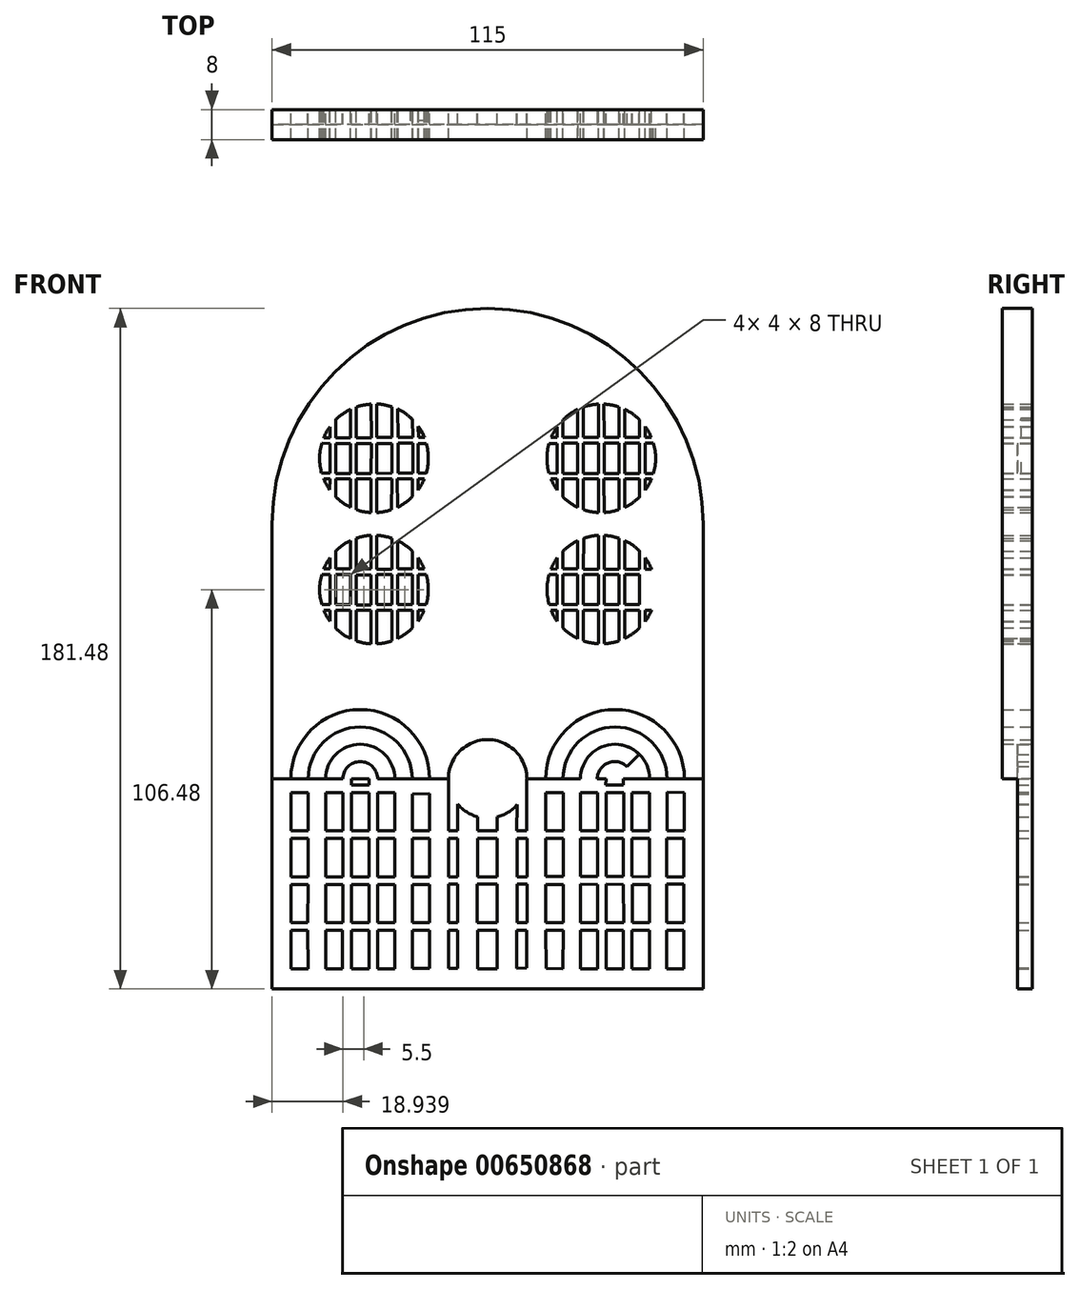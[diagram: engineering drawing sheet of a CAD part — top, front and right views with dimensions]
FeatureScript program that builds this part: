
annotation { "Feature Type Name" : "Feature", "Feature Type Description" : "" }
export const myFeature = defineFeature(function(context is Context, id is Id, definition is map)
    precondition{}
    {
        {
            var Q0;
            Q0=qCreatedBy(makeId("Front.planeOp"),FACE);
            var sketch = newSketch(context, id + "F0", { "sketchPlane" : qUnion([Q0])});
            skCircle(sketch, "E0", {"center": v(0, 0) * mm, "radius": 17.5 * mm});
            skPoint(sketch, "E1", {"position": v(0, 35) * mm});
            skPoint(sketch, "E2", {"position": v(-35, 0) * mm});
            skPoint(sketch, "E3", {"position": v(35, 0) * mm});
            skPoint(sketch, "E4", {"position": v(0, -35) * mm});
            skCircle(sketch, "E5", {"center": v(0, 0) * mm, "radius": 35 * mm});
            skPoint(sketch, "E6", {"position": v(-30.31, 17.5) * mm});
            skPoint(sketch, "E7", {"position": v(30.31, 17.5) * mm});
            skPoint(sketch, "E8", {"position": v(30.31, -17.5) * mm});
            skPoint(sketch, "E9", {"position": v(-30.31, -17.5) * mm});
            skCircle(sketch, "E10", {"center": v(-30.31, 17.5) * mm, "radius": 17.5 * mm});
            skCircle(sketch, "E11", {"center": v(30.31, 17.5) * mm, "radius": 17.5 * mm});
            skPoint(sketch, "E12", {"position": v(15.16, 8.75) * mm});
            skPoint(sketch, "E13", {"position": v(-15.16, -8.75) * mm});
            skCircle(sketch, "E14", {"center": v(-30.31, -17.5) * mm, "radius": 17.5 * mm});
            skCircle(sketch, "E15", {"center": v(0, -35) * mm, "radius": 17.5 * mm});
            skCircle(sketch, "E16", {"center": v(30.31, -17.5) * mm, "radius": 17.5 * mm});
            skCircle(sketch, "E17", {"center": v(0, 35) * mm, "radius": 17.5 * mm});
            skPoint(sketch, "E18", {"position": v(0, -52.5) * mm});
            skCircle(sketch, "E19", {"center": v(0, 0) * mm, "radius": 14.5 * mm});
            skCircle(sketch, "E20", {"center": v(-30.31, 17.5) * mm, "radius": 14.5 * mm});
            skCircle(sketch, "E21", {"center": v(0, 35) * mm, "radius": 14.5 * mm});
            skCircle(sketch, "E22", {"center": v(30.31, 17.5) * mm, "radius": 14.5 * mm});
            skCircle(sketch, "E23", {"center": v(30.31, -17.5) * mm, "radius": 14.5 * mm});
            skCircle(sketch, "E24", {"center": v(0, -35) * mm, "radius": 14.5 * mm});
            skCircle(sketch, "E25", {"center": v(-30.31, -17.5) * mm, "radius": 14.5 * mm});
            skArc(sketch, "E26", {"start": v(57.5, 0) * mm, "mid": v(0, 57.5) * mm, "end": v(-57.5, 0) * mm});
            skPoint(sketch, "E27", {"position": v(-20.96, 36.3) * mm});
            skArc(sketch, "E28", {"start": v(-20.96, 36.3) * mm, "mid": v(-28.74, 38.44) * mm, "end": v(-36.76, 37.49) * mm});
            skArc(sketch, "E29", {"start": v(-20.96, 36.3) * mm, "mid": v(-18.92, 44.11) * mm, "end": v(-14.09, 50.57) * mm});
            skPoint(sketch, "E30", {"position": v(14.09, 50.58) * mm});
            skPoint(sketch, "E31", {"position": v(41.92, 0) * mm});
            skArc(sketch, "E32", {"start": v(50.84, 13.09) * mm, "mid": v(47.66, 5.67) * mm, "end": v(41.92, 0) * mm});
            skArc(sketch, "E33", {"start": v(41.92, 0) * mm, "mid": v(47.66, -5.67) * mm, "end": v(50.84, -13.09) * mm});
            skPoint(sketch, "E34", {"position": v(20.96, 36.3) * mm});
            skArc(sketch, "E35", {"start": v(20.96, 36.3) * mm, "mid": v(28.74, 38.44) * mm, "end": v(36.76, 37.49) * mm});
            skArc(sketch, "E36", {"start": v(14.09, 50.58) * mm, "mid": v(18.92, 44.11) * mm, "end": v(20.96, 36.3) * mm});
            skArc(sketch, "E37", {"start": v(-50.84, -13.09) * mm, "mid": v(-47.66, -5.67) * mm, "end": v(-41.92, 0) * mm});
            skArc(sketch, "E38", {"start": v(-50.84, 13.09) * mm, "mid": v(-47.66, 5.67) * mm, "end": v(-41.92, 0) * mm});
            skArc(sketch, "E39", {"start": v(-50.84, -13.09) * mm, "mid": v(-52.5, 0) * mm, "end": v(-50.84, 13.09) * mm});
            skArc(sketch, "E40", {"start": v(-36.76, -37.49) * mm, "mid": v(-28.74, -38.44) * mm, "end": v(-20.96, -36.3) * mm});
            skArc(sketch, "E41", {"start": v(-20.96, -36.3) * mm, "mid": v(-18.92, -44.11) * mm, "end": v(-14.09, -50.58) * mm});
            skArc(sketch, "E42", {"start": v(-36.76, -37.49) * mm, "mid": v(-26.25, -45.47) * mm, "end": v(-14.09, -50.58) * mm});
            skArc(sketch, "E43", {"start": v(14.09, -50.58) * mm, "mid": v(18.92, -44.11) * mm, "end": v(20.96, -36.3) * mm});
            skArc(sketch, "E44", {"start": v(20.96, -36.3) * mm, "mid": v(28.74, -38.44) * mm, "end": v(36.76, -37.49) * mm});
            skArc(sketch, "E45", {"start": v(14.09, -50.58) * mm, "mid": v(26.25, -45.47) * mm, "end": v(36.76, -37.49) * mm});
            skArc(sketch, "E46", {"start": v(50.84, -13.09) * mm, "mid": v(52.5, 0) * mm, "end": v(50.84, 13.09) * mm, "construction": true});
            skArc(sketch, "E47", {"start": v(14.09, 50.58) * mm, "mid": v(26.25, 45.47) * mm, "end": v(36.76, 37.49) * mm});
            skArc(sketch, "E48", {"start": v(-36.76, 37.49) * mm, "mid": v(-26.25, 45.47) * mm, "end": v(-14.09, 50.58) * mm});
            skLineSegment(sketch, "E49", {"start": v(0, 0) * mm, "end": v(47.13, 81.64) * mm, "construction": true});
            skArc(sketch, "E50", {"start": v(50.84, 13.09) * mm, "mid": v(52.5, 0) * mm, "end": v(50.84, -13.09) * mm});
            skSolve(sketch);
        }
        {
            var Q0;
            Q0=qCreatedBy(makeId("Front.planeOp"),FACE);
            var sketch = newSketch(context, id + "F1", { "sketchPlane" : qUnion([Q0])});
            skArc(sketch, "E51", {"start": v(57.5, 0) * mm, "mid": v(0, 57.5) * mm, "end": v(-57.5, 0) * mm});
            skLineSegment(sketch, "E52", {"start": v(57.5, -67.99) * mm, "end": v(57.5, 0) * mm});
            skLineSegment(sketch, "E53", {"start": v(-57.5, 0) * mm, "end": v(-57.5, -67.99) * mm});
            skPoint(sketch, "E54", {"position": v(-52.5, -67.99) * mm});
            skLineSegment(sketch, "E55", {"start": v(-52.5, -67.99) * mm, "end": v(52.5, -67.99) * mm});
            skPoint(sketch, "E56", {"position": v(-52.5, -23.45) * mm});
            skLineSegment(sketch, "E57", {"start": v(-52.5, -23.45) * mm, "end": v(-52.5, -67.99) * mm});
            skLineSegment(sketch, "E58", {"start": v(52.5, -23.45) * mm, "end": v(52.5, -67.99) * mm});
            skArc(sketch, "E59", {"start": v(-52.5, -23.45) * mm, "mid": v(-31.29, -48.24) * mm, "end": v(0, -57.5) * mm});
            skArc(sketch, "E60", {"start": v(0, -57.5) * mm, "mid": v(31.29, -48.24) * mm, "end": v(52.5, -23.45) * mm});
            skArc(sketch, "E61", {"start": v(-15.48, -67.99) * mm, "mid": v(-33.99, -49.48) * mm, "end": v(-52.5, -67.99) * mm});
            skArc(sketch, "E62", {"start": v(52.5, -67.99) * mm, "mid": v(33.99, -49.48) * mm, "end": v(15.48, -67.99) * mm});
            skArc(sketch, "E63", {"start": v(-10.48, -67.99) * mm, "mid": v(0, -57.5) * mm, "end": v(10.48, -67.99) * mm});
            skLineSegment(sketch, "E64", {"start": v(-10.48, -67.99) * mm, "end": v(-10.48, -73.7) * mm, "construction": true});
            skLineSegment(sketch, "E65", {"start": v(10.48, -67.99) * mm, "end": v(10.48, -74.15) * mm, "construction": true});
            skLineSegment(sketch, "E66", {"start": v(15.48, -67.99) * mm, "end": v(15.48, -73.84) * mm, "construction": true});
            skLineSegment(sketch, "E67", {"start": v(52.5, -67.99) * mm, "end": v(52.5, -74.35) * mm, "construction": true});
            skLineSegment(sketch, "E68", {"start": v(-15.48, -67.99) * mm, "end": v(-15.48, -74.15) * mm, "construction": true});
            skLineSegment(sketch, "E69", {"start": v(-52.5, -67.99) * mm, "end": v(-52.5, -75.2) * mm, "construction": true});
            skLineSegment(sketch, "E70", {"start": v(-15.48, -72) * mm, "end": v(-10.48, -72) * mm, "construction": true});
            skLineSegment(sketch, "E71", {"start": v(10.48, -71.6) * mm, "end": v(15.49, -71.6) * mm, "construction": true});
            skLineSegment(sketch, "E72", {"start": v(52.5, -67.99) * mm, "end": v(57.5, -67.99) * mm, "construction": true});
            skLineSegment(sketch, "E73", {"start": v(-52.5, -67.99) * mm, "end": v(-57.5, -67.99) * mm, "construction": true});
            skCircle(sketch, "E74", {"center": v(0, 0) * mm, "radius": 57.5 * mm});
            skLineSegment(sketch, "E75", {"start": v(15.49, -71.6) * mm, "end": v(20.11, -71.6) * mm, "construction": true});
            skLineSegment(sketch, "E76", {"start": v(20.11, -71.6) * mm, "end": v(24.74, -71.6) * mm, "construction": true});
            skLineSegment(sketch, "E77", {"start": v(24.74, -71.6) * mm, "end": v(29.36, -71.6) * mm, "construction": true});
            skLineSegment(sketch, "E78", {"start": v(29.36, -71.6) * mm, "end": v(33.99, -71.6) * mm, "construction": true});
            skLineSegment(sketch, "E79", {"start": v(33.99, -71.6) * mm, "end": v(38.62, -71.6) * mm, "construction": true});
            skLineSegment(sketch, "E80", {"start": v(38.62, -71.6) * mm, "end": v(43.24, -71.6) * mm, "construction": true});
            skLineSegment(sketch, "E81", {"start": v(43.24, -71.6) * mm, "end": v(47.87, -71.6) * mm, "construction": true});
            skLineSegment(sketch, "E82", {"start": v(47.87, -71.6) * mm, "end": v(52.5, -71.6) * mm, "construction": true});
            skLineSegment(sketch, "E83", {"start": v(20.11, -71.6) * mm, "end": v(20.11, -67.99) * mm, "construction": true});
            skLineSegment(sketch, "E84", {"start": v(24.74, -71.6) * mm, "end": v(24.74, -67.99) * mm, "construction": true});
            skLineSegment(sketch, "E85", {"start": v(29.36, -71.6) * mm, "end": v(29.36, -67.99) * mm, "construction": true});
            skLineSegment(sketch, "E86", {"start": v(33.99, -71.6) * mm, "end": v(33.99, -67.99) * mm, "construction": true});
            skLineSegment(sketch, "E87", {"start": v(38.62, -71.6) * mm, "end": v(38.62, -67.99) * mm, "construction": true});
            skLineSegment(sketch, "E88", {"start": v(43.24, -71.6) * mm, "end": v(43.24, -67.99) * mm, "construction": true});
            skLineSegment(sketch, "E89", {"start": v(47.87, -71.6) * mm, "end": v(47.87, -67.99) * mm, "construction": true});
            skArc(sketch, "E90", {"start": v(47.87, -67.99) * mm, "mid": v(33.99, -54.1) * mm, "end": v(20.11, -67.99) * mm});
            skArc(sketch, "E91", {"start": v(43.24, -67.99) * mm, "mid": v(33.99, -58.74) * mm, "end": v(24.74, -67.99) * mm});
            skArc(sketch, "E92", {"start": v(38.62, -67.99) * mm, "mid": v(33.99, -63.36) * mm, "end": v(29.36, -67.99) * mm});
            skLineSegment(sketch, "E93", {"start": v(-15.48, -72) * mm, "end": v(-20.11, -72) * mm, "construction": true});
            skLineSegment(sketch, "E94", {"start": v(-20.11, -72) * mm, "end": v(-24.74, -72) * mm, "construction": true});
            skLineSegment(sketch, "E95", {"start": v(-24.74, -72) * mm, "end": v(-29.36, -72) * mm, "construction": true});
            skLineSegment(sketch, "E96", {"start": v(-29.36, -72) * mm, "end": v(-33.99, -72) * mm, "construction": true});
            skLineSegment(sketch, "E97", {"start": v(-33.99, -72) * mm, "end": v(-38.62, -72) * mm, "construction": true});
            skLineSegment(sketch, "E98", {"start": v(-38.62, -72) * mm, "end": v(-43.24, -72) * mm, "construction": true});
            skLineSegment(sketch, "E99", {"start": v(-43.24, -72) * mm, "end": v(-47.87, -72) * mm, "construction": true});
            skLineSegment(sketch, "E100", {"start": v(-47.87, -72) * mm, "end": v(-52.5, -72) * mm, "construction": true});
            skLineSegment(sketch, "E101", {"start": v(-47.87, -72) * mm, "end": v(-47.87, -67.99) * mm, "construction": true});
            skLineSegment(sketch, "E102", {"start": v(-43.24, -72) * mm, "end": v(-43.24, -67.99) * mm, "construction": true});
            skLineSegment(sketch, "E103", {"start": v(-38.62, -72) * mm, "end": v(-38.62, -67.99) * mm, "construction": true});
            skLineSegment(sketch, "E104", {"start": v(-29.36, -72) * mm, "end": v(-29.36, -67.99) * mm, "construction": true});
            skLineSegment(sketch, "E105", {"start": v(-24.74, -72) * mm, "end": v(-24.74, -67.99) * mm, "construction": true});
            skLineSegment(sketch, "E106", {"start": v(-20.11, -72) * mm, "end": v(-20.11, -67.99) * mm, "construction": true});
            skLineSegment(sketch, "E107", {"start": v(-33.99, -72) * mm, "end": v(-33.99, -67.99) * mm, "construction": true});
            skArc(sketch, "E108", {"start": v(-20.11, -67.99) * mm, "mid": v(-33.99, -54.1) * mm, "end": v(-47.87, -67.99) * mm});
            skArc(sketch, "E109", {"start": v(-24.74, -67.99) * mm, "mid": v(-33.99, -58.74) * mm, "end": v(-43.24, -67.99) * mm});
            skArc(sketch, "E110", {"start": v(-29.36, -67.99) * mm, "mid": v(-33.99, -63.36) * mm, "end": v(-38.62, -67.99) * mm});
            skLineSegment(sketch, "E111", {"start": v(-10.48, -72) * mm, "end": v(-7.86, -72) * mm, "construction": true});
            skLineSegment(sketch, "E112", {"start": v(-7.86, -72) * mm, "end": v(-5.24, -72) * mm, "construction": true});
            skLineSegment(sketch, "E113", {"start": v(-5.24, -72) * mm, "end": v(-2.62, -72) * mm, "construction": true});
            skLineSegment(sketch, "E114", {"start": v(-2.62, -72) * mm, "end": v(0, -72) * mm, "construction": true});
            skLineSegment(sketch, "E115", {"start": v(0, -72) * mm, "end": v(2.62, -72) * mm, "construction": true});
            skLineSegment(sketch, "E116", {"start": v(2.62, -72) * mm, "end": v(5.24, -72) * mm, "construction": true});
            skLineSegment(sketch, "E117", {"start": v(5.24, -72) * mm, "end": v(7.86, -72) * mm, "construction": true});
            skLineSegment(sketch, "E118", {"start": v(7.86, -72) * mm, "end": v(10.48, -72) * mm, "construction": true});
            skLineSegment(sketch, "E119", {"start": v(-7.86, -72) * mm, "end": v(-7.86, -67.99) * mm, "construction": true});
            skLineSegment(sketch, "E120", {"start": v(-5.24, -72) * mm, "end": v(-5.24, -67.99) * mm, "construction": true});
            skLineSegment(sketch, "E121", {"start": v(-2.62, -72) * mm, "end": v(-2.62, -67.99) * mm, "construction": true});
            skLineSegment(sketch, "E122", {"start": v(2.62, -72) * mm, "end": v(2.62, -67.99) * mm, "construction": true});
            skLineSegment(sketch, "E123", {"start": v(0, -72) * mm, "end": v(0, -67.98) * mm, "construction": true});
            skLineSegment(sketch, "E124", {"start": v(5.24, -72) * mm, "end": v(5.24, -67.99) * mm, "construction": true});
            skLineSegment(sketch, "E125", {"start": v(7.86, -72) * mm, "end": v(7.86, -67.99) * mm, "construction": true});
            skArc(sketch, "E126", {"start": v(7.86, -67.99) * mm, "mid": v(0, -60.13) * mm, "end": v(-7.86, -67.99) * mm});
            skArc(sketch, "E127", {"start": v(5.24, -67.99) * mm, "mid": v(0, -62.75) * mm, "end": v(-5.24, -67.99) * mm});
            skArc(sketch, "E128", {"start": v(2.62, -67.99) * mm, "mid": v(0, -65.37) * mm, "end": v(-2.62, -67.99) * mm});
            skLineSegment(sketch, "E129", {"start": v(-33.99, -67.99) * mm, "end": v(-33.99, -49.48) * mm, "construction": true});
            skLineSegment(sketch, "E130", {"start": v(33.99, -67.99) * mm, "end": v(33.99, -49.48) * mm, "construction": true});
            skLineSegment(sketch, "E131", {"start": v(0, -57.5) * mm, "end": v(0, -67.98) * mm, "construction": true});
            skLineSegment(sketch, "E132", {"start": v(-33.99, -67.99) * mm, "end": v(-47.08, -54.9) * mm, "construction": true});
            skLineSegment(sketch, "E133", {"start": v(-33.99, -67.99) * mm, "end": v(-20.9, -54.9) * mm, "construction": true});
            skLineSegment(sketch, "E134", {"start": v(33.99, -67.99) * mm, "end": v(20.9, -54.9) * mm, "construction": true});
            skLineSegment(sketch, "E135", {"start": v(33.99, -67.99) * mm, "end": v(47.08, -54.9) * mm, "construction": true});
            skLineSegment(sketch, "E136", {"start": v(0, -67.98) * mm, "end": v(7.41, -60.57) * mm, "construction": true});
            skLineSegment(sketch, "E137", {"start": v(0, -67.98) * mm, "end": v(-7.41, -60.57) * mm, "construction": true});
            skLineSegment(sketch, "E138", {"start": v(-57.5, -67.99) * mm, "end": v(-52.5, -67.99) * mm});
            skLineSegment(sketch, "E139", {"start": v(52.5, -67.99) * mm, "end": v(57.5, -67.99) * mm});
            skPoint(sketch, "E140", {"position": v(-29.56, -3.02) * mm});
            skPoint(sketch, "E141", {"position": v(-42.06, -21.5) * mm});
            skLineSegment(sketch, "E142.bottom", {"start": v(-40.56, -13.5) * mm, "end": v(-40.56, -13.5) * mm});
            skLineSegment(sketch, "E142.top", {"start": v(-40.56, -21.5) * mm, "end": v(-40.56, -21.5) * mm});
            skLineSegment(sketch, "E142.left", {"start": v(-40.56, -13.5) * mm, "end": v(-40.56, -21.5) * mm});
            skLineSegment(sketch, "E142.right", {"start": v(-40.56, -13.5) * mm, "end": v(-40.56, -21.5) * mm});
            skLineSegment(sketch, "E143.bottom", {"start": v(-36.56, -21.5) * mm, "end": v(-36.57, -21.5) * mm});
            skLineSegment(sketch, "E143.top", {"start": v(-36.56, -13.5) * mm, "end": v(-36.57, -13.5) * mm});
            skLineSegment(sketch, "E143.left", {"start": v(-36.57, -21.5) * mm, "end": v(-36.57, -13.5) * mm});
            skLineSegment(sketch, "E143.right", {"start": v(-36.56, -21.5) * mm, "end": v(-36.56, -13.5) * mm});
            skLineSegment(sketch, "E144.bottom", {"start": v(-35.06, -13.56) * mm, "end": v(-31.06, -13.56) * mm});
            skLineSegment(sketch, "E144.top", {"start": v(-35.06, -21.56) * mm, "end": v(-31.06, -21.56) * mm});
            skLineSegment(sketch, "E144.left", {"start": v(-35.06, -13.56) * mm, "end": v(-35.06, -21.56) * mm});
            skLineSegment(sketch, "E144.right", {"start": v(-31.06, -13.56) * mm, "end": v(-31.06, -21.56) * mm});
            skLineSegment(sketch, "E145.bottom", {"start": v(-29.56, -13.52) * mm, "end": v(-25.56, -13.52) * mm});
            skLineSegment(sketch, "E145.top", {"start": v(-29.56, -21.52) * mm, "end": v(-25.56, -21.52) * mm});
            skLineSegment(sketch, "E145.left", {"start": v(-29.56, -13.52) * mm, "end": v(-29.56, -21.52) * mm});
            skLineSegment(sketch, "E145.right", {"start": v(-25.56, -13.52) * mm, "end": v(-25.56, -21.52) * mm});
            skLineSegment(sketch, "E146.bottom", {"start": v(-24.06, -13.5) * mm, "end": v(-20.06, -13.5) * mm});
            skLineSegment(sketch, "E146.top", {"start": v(-24.06, -21.5) * mm, "end": v(-20.06, -21.5) * mm});
            skLineSegment(sketch, "E146.left", {"start": v(-24.06, -13.5) * mm, "end": v(-24.06, -21.5) * mm});
            skLineSegment(sketch, "E146.right", {"start": v(-20.06, -13.5) * mm, "end": v(-20.06, -21.5) * mm});
            skLineSegment(sketch, "E147.bottom", {"start": v(-40.56, -13.5) * mm, "end": v(-36.57, -13.5) * mm});
            skLineSegment(sketch, "E147.top", {"start": v(-40.56, -21.5) * mm, "end": v(-36.57, -21.5) * mm});
            skLineSegment(sketch, "E147.right", {"start": v(-36.57, -13.5) * mm, "end": v(-36.57, -21.5) * mm});
            skLineSegment(sketch, "E148.bottom", {"start": v(-35.06, -23) * mm, "end": v(-31.06, -23) * mm});
            skLineSegment(sketch, "E149.bottom", {"start": v(-29.56, -23) * mm, "end": v(-25.57, -23) * mm});
            skLineSegment(sketch, "E150", {"start": v(-40.56, -13.5) * mm, "end": v(-36.56, -13.5) * mm});
            skLineSegment(sketch, "E151", {"start": v(-40.56, -12) * mm, "end": v(-36.56, -12) * mm});
            skLineSegment(sketch, "E152", {"start": v(-29.56, -12.02) * mm, "end": v(-25.56, -12.02) * mm});
            skLineSegment(sketch, "E153", {"start": v(-24.06, -12) * mm, "end": v(-20.06, -12) * mm});
            skLineSegment(sketch, "E154", {"start": v(-35.3, -3.87) * mm, "end": v(-35.3, -3.86) * mm});
            skLineSegment(sketch, "E155", {"start": v(-40.56, -23) * mm, "end": v(-36.56, -23) * mm});
            skLineSegment(sketch, "E156", {"start": v(-44.24, -13.5) * mm, "end": v(-42.06, -13.5) * mm});
            skLineSegment(sketch, "E157", {"start": v(-42.06, -13.5) * mm, "end": v(-42.06, -21.5) * mm});
            skLineSegment(sketch, "E158", {"start": v(-18.56, -21.5) * mm, "end": v(-16.38, -21.5) * mm});
            skLineSegment(sketch, "E159", {"start": v(-18.56, -13.52) * mm, "end": v(-18.56, -21.5) * mm});
            skPoint(sketch, "E160", {"position": v(0, -124.5) * mm});
            skLineSegment(sketch, "E161", {"start": v(57.5, -124.17) * mm, "end": v(-57.5, -124.17) * mm});
            skArc(sketch, "E162", {"start": v(-44.24, -13.5) * mm, "mid": v(-44.8, -17.5) * mm, "end": v(-44.24, -21.51) * mm});
            skArc(sketch, "E163", {"start": v(-16.4, -13.5) * mm, "mid": v(-15.83, -17.5) * mm, "end": v(-16.39, -21.5) * mm});
            skPoint(sketch, "E164", {"position": v(-44.24, -21.5) * mm});
            skLineSegment(sketch, "E165", {"start": v(-44.24, -21.5) * mm, "end": v(-42.06, -21.5) * mm});
            skPoint(sketch, "E166", {"position": v(-36.56, -12) * mm});
            skLineSegment(sketch, "E167", {"start": v(-35.06, -12) * mm, "end": v(-31.06, -12) * mm});
            skPoint(sketch, "E168", {"position": v(-35.07, -3.8) * mm});
            skPoint(sketch, "E169", {"position": v(-31.07, -3.02) * mm});
            skArc(sketch, "E170", {"start": v(-35.07, -3.8) * mm, "mid": v(-33.1, -3.28) * mm, "end": v(-31.07, -3.03) * mm});
            skArc(sketch, "E171", {"start": v(-29.56, -3.02) * mm, "mid": v(-27.53, -3.27) * mm, "end": v(-25.56, -3.8) * mm});
            skPoint(sketch, "E172", {"position": v(-36.57, -4.42) * mm});
            skPoint(sketch, "E173", {"position": v(-24.06, -4.41) * mm});
            skLineSegment(sketch, "E174", {"start": v(-20.07, -7.24) * mm, "end": v(-20.06, -12) * mm});
            skPoint(sketch, "E175", {"position": v(-18.57, -12) * mm});
            skPoint(sketch, "E176", {"position": v(-18.56, -9.01) * mm});
            skPoint(sketch, "E177", {"position": v(-16.92, -12) * mm});
            skLineSegment(sketch, "E178", {"start": v(-18.56, -9.01) * mm, "end": v(-18.57, -12) * mm});
            skPoint(sketch, "E179", {"position": v(-42.06, -9) * mm});
            skPoint(sketch, "E180", {"position": v(-42.06, -12) * mm});
            skPoint(sketch, "E181", {"position": v(-43.72, -12) * mm});
            skLineSegment(sketch, "E182", {"start": v(-43.72, -12) * mm, "end": v(-42.06, -12) * mm});
            skLineSegment(sketch, "E183", {"start": v(-42.06, -12) * mm, "end": v(-42.06, -9) * mm});
            skArc(sketch, "E184", {"start": v(-43.72, -12) * mm, "mid": v(-42.98, -10.47) * mm, "end": v(-42.06, -9.03) * mm});
            skArc(sketch, "E185", {"start": v(-18.56, -9.01) * mm, "mid": v(-17.64, -10.46) * mm, "end": v(-16.9, -12) * mm});
            skPoint(sketch, "E186", {"position": v(-42.06, -25.98) * mm});
            skPoint(sketch, "E187", {"position": v(-42.09, -23) * mm});
            skPoint(sketch, "E188", {"position": v(-43.7, -23) * mm});
            skLineSegment(sketch, "E189", {"start": v(-43.7, -23) * mm, "end": v(-42.09, -23) * mm});
            skLineSegment(sketch, "E190", {"start": v(-42.09, -23) * mm, "end": v(-42.06, -25.98) * mm});
            skArc(sketch, "E191", {"start": v(-43.7, -23) * mm, "mid": v(-42.97, -24.52) * mm, "end": v(-42.06, -25.94) * mm});
            skPoint(sketch, "E192", {"position": v(-31.07, -31.97) * mm});
            skPoint(sketch, "E193", {"position": v(-25.56, -31.19) * mm});
            skPoint(sketch, "E194", {"position": v(-20.06, -27.74) * mm});
            skLineSegment(sketch, "E195", {"start": v(-24.06, -23) * mm, "end": v(-20.06, -23) * mm});
            skPoint(sketch, "E196", {"position": v(-18.56, -22.98) * mm});
            skPoint(sketch, "E197", {"position": v(-16.92, -22.98) * mm});
            skPoint(sketch, "E198", {"position": v(-18.56, -25.95) * mm});
            skLineSegment(sketch, "E199", {"start": v(-18.56, -25.95) * mm, "end": v(-18.56, -22.98) * mm});
            skArc(sketch, "E200", {"start": v(-16.92, -22.98) * mm, "mid": v(-17.65, -24.51) * mm, "end": v(-18.56, -25.95) * mm});
            skLineSegment(sketch, "E201", {"start": v(-18.56, -22.98) * mm, "end": v(-16.92, -22.98) * mm});
            skPoint(sketch, "E202", {"position": v(-35.06, -31.2) * mm});
            skLineSegment(sketch, "E203", {"start": v(-18.57, -12) * mm, "end": v(-16.9, -12) * mm});
            skPoint(sketch, "E204", {"position": v(-24.06, -30.58) * mm});
            skArc(sketch, "E205", {"start": v(-31.07, -31.97) * mm, "mid": v(-33.1, -31.72) * mm, "end": v(-35.06, -31.2) * mm});
            skPoint(sketch, "E206", {"position": v(-29.56, -31.97) * mm});
            skArc(sketch, "E207", {"start": v(-25.56, -31.19) * mm, "mid": v(-27.53, -31.72) * mm, "end": v(-29.56, -31.97) * mm});
            skLineSegment(sketch, "E208", {"start": v(-35.07, -3.8) * mm, "end": v(-35.06, -12) * mm});
            skLineSegment(sketch, "E209", {"start": v(-31.07, -3.02) * mm, "end": v(-31.06, -12) * mm});
            skLineSegment(sketch, "E210", {"start": v(-29.56, -3.02) * mm, "end": v(-29.56, -12.02) * mm});
            skPoint(sketch, "E211", {"position": v(-25.56, -3.8) * mm});
            skLineSegment(sketch, "E212", {"start": v(-25.56, -3.8) * mm, "end": v(-25.56, -12.02) * mm});
            skPoint(sketch, "E213", {"position": v(-40.56, -7.25) * mm});
            skLineSegment(sketch, "E214", {"start": v(-36.57, -4.42) * mm, "end": v(-36.56, -12) * mm});
            skLineSegment(sketch, "E215", {"start": v(-40.56, -7.25) * mm, "end": v(-40.56, -12) * mm});
            skArc(sketch, "E216", {"start": v(-40.56, -7.25) * mm, "mid": v(-38.69, -5.66) * mm, "end": v(-36.57, -4.42) * mm});
            skArc(sketch, "E217", {"start": v(-24.06, -4.41) * mm, "mid": v(-21.94, -5.66) * mm, "end": v(-20.07, -7.25) * mm});
            skLineSegment(sketch, "E218", {"start": v(-24.06, -4.41) * mm, "end": v(-24.06, -12) * mm});
            skLineSegment(sketch, "E219", {"start": v(-20.07, -7.25) * mm, "end": v(-20.06, -12) * mm});
            skPoint(sketch, "E220", {"position": v(-40.56, -27.75) * mm});
            skPoint(sketch, "E221", {"position": v(-36.57, -30.57) * mm});
            skLineSegment(sketch, "E222", {"start": v(-40.56, -23) * mm, "end": v(-40.56, -27.75) * mm});
            skLineSegment(sketch, "E223", {"start": v(-36.56, -23) * mm, "end": v(-36.57, -30.57) * mm});
            skArc(sketch, "E224", {"start": v(-40.56, -27.75) * mm, "mid": v(-38.69, -29.33) * mm, "end": v(-36.57, -30.57) * mm});
            skLineSegment(sketch, "E225", {"start": v(-35.06, -23) * mm, "end": v(-35.06, -31.2) * mm});
            skLineSegment(sketch, "E226", {"start": v(-31.06, -23) * mm, "end": v(-31.07, -31.97) * mm});
            skLineSegment(sketch, "E227", {"start": v(-29.56, -23) * mm, "end": v(-29.56, -31.97) * mm});
            skLineSegment(sketch, "E228", {"start": v(-25.57, -23) * mm, "end": v(-25.56, -31.19) * mm});
            skLineSegment(sketch, "E229", {"start": v(-24.06, -23) * mm, "end": v(-24.06, -30.58) * mm});
            skLineSegment(sketch, "E230", {"start": v(-20.06, -23) * mm, "end": v(-20.06, -27.74) * mm});
            skArc(sketch, "E231", {"start": v(-20.06, -27.74) * mm, "mid": v(-21.94, -29.32) * mm, "end": v(-24.06, -30.57) * mm});
            skPoint(sketch, "E232", {"position": v(-42.1, 21.5) * mm});
            skPoint(sketch, "E233", {"position": v(-44.82, 17.5) * mm});
            skPoint(sketch, "E234", {"position": v(-42.08, 17.5) * mm});
            skPoint(sketch, "E235", {"position": v(-40.57, 17.5) * mm});
            skPoint(sketch, "E236", {"position": v(-42.07, 23) * mm});
            skPoint(sketch, "E237", {"position": v(-44.24, 21.53) * mm});
            skPoint(sketch, "E238", {"position": v(-43.74, 23) * mm});
            skLineSegment(sketch, "E239", {"start": v(-43.74, 23) * mm, "end": v(-42.07, 23) * mm});
            skLineSegment(sketch, "E240", {"start": v(-44.24, 21.53) * mm, "end": v(-42.1, 21.5) * mm});
            skLineSegment(sketch, "E241", {"start": v(-40.57, 23) * mm, "end": v(-36.56, 23) * mm});
            skLineSegment(sketch, "E242", {"start": v(-40.57, 21.5) * mm, "end": v(-36.56, 21.5) * mm});
            skLineSegment(sketch, "E243", {"start": v(-35.07, 23.04) * mm, "end": v(-31.04, 23.04) * mm});
            skLineSegment(sketch, "E244", {"start": v(-35.07, 21.5) * mm, "end": v(-31.04, 21.5) * mm});
            skLineSegment(sketch, "E245", {"start": v(-35.07, 31.2) * mm, "end": v(-35.07, 23.04) * mm});
            skLineSegment(sketch, "E246", {"start": v(-36.54, 30.6) * mm, "end": v(-36.56, 23) * mm});
            skPoint(sketch, "E247", {"position": v(-40.56, 27.8) * mm});
            skPoint(sketch, "E248", {"position": v(-42.08, 25.99) * mm});
            skLineSegment(sketch, "E249", {"start": v(-40.56, 27.8) * mm, "end": v(-40.57, 23) * mm});
            skLineSegment(sketch, "E250", {"start": v(-42.08, 25.99) * mm, "end": v(-42.07, 23) * mm});
            skPoint(sketch, "E251", {"position": v(-40.57, 13.5) * mm});
            skPoint(sketch, "E252", {"position": v(-36.58, 13.5) * mm});
            skPoint(sketch, "E253", {"position": v(-35.07, 13.5) * mm});
            skPoint(sketch, "E254", {"position": v(-31.08, 13.5) * mm});
            skPoint(sketch, "E255", {"position": v(-29.54, 13.5) * mm});
            skLineSegment(sketch, "E256", {"start": v(-40.57, 21.5) * mm, "end": v(-40.57, 13.5) * mm});
            skLineSegment(sketch, "E257", {"start": v(-36.56, 21.5) * mm, "end": v(-36.58, 13.5) * mm});
            skLineSegment(sketch, "E258", {"start": v(-35.07, 21.5) * mm, "end": v(-35.07, 13.5) * mm});
            skLineSegment(sketch, "E259", {"start": v(-31.04, 21.5) * mm, "end": v(-31.08, 13.5) * mm});
            skLineSegment(sketch, "E260", {"start": v(-40.57, 13.5) * mm, "end": v(-36.58, 13.5) * mm});
            skLineSegment(sketch, "E261", {"start": v(-35.07, 13.5) * mm, "end": v(-31.08, 13.5) * mm});
            skPoint(sketch, "E262", {"position": v(-44.27, 13.52) * mm});
            skPoint(sketch, "E263", {"position": v(-42.07, 13.52) * mm});
            skLineSegment(sketch, "E264", {"start": v(-44.27, 13.52) * mm, "end": v(-42.07, 13.52) * mm});
            skPoint(sketch, "E265", {"position": v(-29.6, 23.04) * mm});
            skPoint(sketch, "E266", {"position": v(-29.6, 21.5) * mm});
            skPoint(sketch, "E267", {"position": v(-25.47, 23.1) * mm});
            skPoint(sketch, "E268", {"position": v(-23.93, 23.1) * mm});
            skPoint(sketch, "E269", {"position": v(-19.94, 23.1) * mm});
            skPoint(sketch, "E270", {"position": v(-16.82, 23.1) * mm});
            skPoint(sketch, "E271", {"position": v(-18.46, 23.1) * mm});
            skPoint(sketch, "E272", {"position": v(-25.47, 21.5) * mm});
            skPoint(sketch, "E273", {"position": v(-23.93, 21.55) * mm});
            skPoint(sketch, "E274", {"position": v(-19.94, 21.55) * mm});
            skPoint(sketch, "E275", {"position": v(-18.57, 21.5) * mm});
            skPoint(sketch, "E276", {"position": v(-16.39, 21.5) * mm});
            skPoint(sketch, "E277", {"position": v(-25.47, 13.58) * mm});
            skPoint(sketch, "E278", {"position": v(-23.93, 13.58) * mm});
            skPoint(sketch, "E279", {"position": v(-19.94, 13.58) * mm});
            skPoint(sketch, "E280", {"position": v(-18.57, 13.52) * mm});
            skPoint(sketch, "E281", {"position": v(-16.35, 13.53) * mm});
            skLineSegment(sketch, "E282", {"start": v(-29.6, 23.04) * mm, "end": v(-25.47, 23.1) * mm});
            skLineSegment(sketch, "E283", {"start": v(-23.93, 23.1) * mm, "end": v(-19.94, 23.1) * mm});
            skLineSegment(sketch, "E284", {"start": v(-18.46, 23.1) * mm, "end": v(-16.82, 23.1) * mm});
            skLineSegment(sketch, "E285", {"start": v(-29.6, 21.5) * mm, "end": v(-25.47, 21.5) * mm});
            skLineSegment(sketch, "E286", {"start": v(-23.93, 21.55) * mm, "end": v(-19.94, 21.55) * mm});
            skLineSegment(sketch, "E287", {"start": v(-18.57, 21.5) * mm, "end": v(-16.39, 21.5) * mm});
            skLineSegment(sketch, "E288", {"start": v(-29.54, 13.5) * mm, "end": v(-25.47, 13.58) * mm});
            skLineSegment(sketch, "E289", {"start": v(-23.93, 13.58) * mm, "end": v(-19.94, 13.58) * mm});
            skLineSegment(sketch, "E290", {"start": v(-29.6, 21.5) * mm, "end": v(-29.54, 13.5) * mm});
            skLineSegment(sketch, "E291", {"start": v(-25.47, 21.5) * mm, "end": v(-25.47, 13.58) * mm});
            skLineSegment(sketch, "E292", {"start": v(-23.93, 21.55) * mm, "end": v(-23.93, 13.58) * mm});
            skLineSegment(sketch, "E293", {"start": v(-19.94, 21.55) * mm, "end": v(-19.94, 13.58) * mm});
            skLineSegment(sketch, "E294", {"start": v(-18.57, 21.5) * mm, "end": v(-18.57, 13.52) * mm});
            skPoint(sketch, "E295", {"position": v(-40.57, 12) * mm});
            skPoint(sketch, "E296", {"position": v(-36.59, 12.05) * mm});
            skPoint(sketch, "E297", {"position": v(-35.07, 12.05) * mm});
            skPoint(sketch, "E298", {"position": v(-31.08, 12.05) * mm});
            skPoint(sketch, "E299", {"position": v(-29.56, 12.05) * mm});
            skPoint(sketch, "E300", {"position": v(-25.55, 12.05) * mm});
            skPoint(sketch, "E301", {"position": v(-24.08, 12.05) * mm});
            skPoint(sketch, "E302", {"position": v(-20.06, 12.05) * mm});
            skPoint(sketch, "E303", {"position": v(-18.6, 12.05) * mm});
            skPoint(sketch, "E304", {"position": v(-16.9, 12.05) * mm});
            skPoint(sketch, "E305", {"position": v(-40.57, 7.3) * mm});
            skPoint(sketch, "E306", {"position": v(-36.6, 4.43) * mm});
            skPoint(sketch, "E307", {"position": v(-35.09, 3.8) * mm});
            skPoint(sketch, "E308", {"position": v(-31.1, 3.06) * mm});
            skPoint(sketch, "E309", {"position": v(-29.56, 3.05) * mm});
            skPoint(sketch, "E310", {"position": v(-25.6, 3.8) * mm});
            skPoint(sketch, "E311", {"position": v(-24.05, 4.43) * mm});
            skPoint(sketch, "E312", {"position": v(-20.07, 7.3) * mm});
            skPoint(sketch, "E313", {"position": v(-18.54, 9.06) * mm});
            skLineSegment(sketch, "E314", {"start": v(-40.57, 12) * mm, "end": v(-36.59, 12.05) * mm});
            skLineSegment(sketch, "E315", {"start": v(-35.07, 12.05) * mm, "end": v(-31.08, 12.05) * mm});
            skLineSegment(sketch, "E316", {"start": v(-29.56, 12.05) * mm, "end": v(-25.55, 12.05) * mm});
            skLineSegment(sketch, "E317", {"start": v(-24.08, 12.05) * mm, "end": v(-20.06, 12.05) * mm});
            skLineSegment(sketch, "E318", {"start": v(-18.6, 12.05) * mm, "end": v(-16.9, 12.05) * mm});
            skLineSegment(sketch, "E319", {"start": v(-40.57, 12) * mm, "end": v(-40.57, 7.3) * mm});
            skLineSegment(sketch, "E320", {"start": v(-36.59, 12.05) * mm, "end": v(-36.6, 4.43) * mm});
            skLineSegment(sketch, "E321", {"start": v(-35.07, 12.05) * mm, "end": v(-35.09, 3.8) * mm});
            skLineSegment(sketch, "E322", {"start": v(-31.08, 12.05) * mm, "end": v(-31.1, 3.06) * mm});
            skLineSegment(sketch, "E323", {"start": v(-29.56, 12.05) * mm, "end": v(-29.56, 3.05) * mm});
            skLineSegment(sketch, "E324", {"start": v(-25.55, 12.05) * mm, "end": v(-25.6, 3.8) * mm});
            skLineSegment(sketch, "E325", {"start": v(-24.08, 12.05) * mm, "end": v(-24.05, 4.43) * mm});
            skLineSegment(sketch, "E326", {"start": v(-20.06, 12.05) * mm, "end": v(-20.07, 7.3) * mm});
            skLineSegment(sketch, "E327", {"start": v(-18.6, 12.05) * mm, "end": v(-18.54, 9.06) * mm});
            skPoint(sketch, "E328", {"position": v(-29.58, 32.04) * mm});
            skPoint(sketch, "E329", {"position": v(-25.55, 31.25) * mm});
            skPoint(sketch, "E330", {"position": v(-23.98, 30.68) * mm});
            skPoint(sketch, "E331", {"position": v(-18.49, 26.07) * mm});
            skLineSegment(sketch, "E332", {"start": v(-29.58, 32.04) * mm, "end": v(-29.6, 23.04) * mm});
            skLineSegment(sketch, "E333", {"start": v(-23.98, 30.68) * mm, "end": v(-23.93, 23.1) * mm});
            skLineSegment(sketch, "E334", {"start": v(-18.49, 26.07) * mm, "end": v(-18.46, 23.1) * mm});
            skArc(sketch, "E335", {"start": v(-44.27, 13.52) * mm, "mid": v(-44.81, 17.53) * mm, "end": v(-44.22, 21.53) * mm});
            skArc(sketch, "E336", {"start": v(-43.74, 23) * mm, "mid": v(-43, 24.53) * mm, "end": v(-42.08, 25.96) * mm});
            skArc(sketch, "E337", {"start": v(-40.56, 27.8) * mm, "mid": v(-38.67, 29.37) * mm, "end": v(-36.54, 30.6) * mm});
            skArc(sketch, "E338", {"start": v(-35.07, 31.2) * mm, "mid": v(-33.1, 31.71) * mm, "end": v(-31.08, 31.95) * mm});
            skArc(sketch, "E339", {"start": v(-29.58, 32.04) * mm, "mid": v(-27.56, 31.79) * mm, "end": v(-25.6, 31.25) * mm});
            skArc(sketch, "E340", {"start": v(-23.98, 30.68) * mm, "mid": v(-21.88, 29.43) * mm, "end": v(-20.01, 27.86) * mm});
            skArc(sketch, "E341", {"start": v(-18.49, 26.07) * mm, "mid": v(-17.57, 24.63) * mm, "end": v(-16.82, 23.1) * mm});
            skArc(sketch, "E342", {"start": v(-16.39, 21.5) * mm, "mid": v(-15.81, 17.52) * mm, "end": v(-16.35, 13.53) * mm});
            skArc(sketch, "E343", {"start": v(-44.22, 21.53) * mm, "mid": v(-44.81, 17.53) * mm, "end": v(-44.27, 13.52) * mm});
            skArc(sketch, "E344", {"start": v(-40.57, 7.3) * mm, "mid": v(-38.7, 5.72) * mm, "end": v(-36.6, 4.48) * mm});
            skArc(sketch, "E345", {"start": v(-29.56, 3.05) * mm, "mid": v(-27.55, 3.3) * mm, "end": v(-25.6, 3.85) * mm});
            skArc(sketch, "E346", {"start": v(-24.05, 4.43) * mm, "mid": v(-21.94, 5.7) * mm, "end": v(-20.07, 7.3) * mm});
            skArc(sketch, "E347", {"start": v(-18.54, 9.06) * mm, "mid": v(-17.64, 10.5) * mm, "end": v(-16.9, 12.05) * mm});
            skLineSegment(sketch, "E348", {"start": v(-42.1, 21.5) * mm, "end": v(-42.07, 13.52) * mm});
            skLineSegment(sketch, "E349", {"start": v(-20.01, 27.86) * mm, "end": v(-19.94, 23.1) * mm});
            skLineSegment(sketch, "E350", {"start": v(-25.55, 31.25) * mm, "end": v(-25.47, 23.1) * mm});
            skLineSegment(sketch, "E351", {"start": v(-31.08, 31.95) * mm, "end": v(-31.04, 23.04) * mm});
            skArc(sketch, "E352", {"start": v(-29.58, 32.04) * mm, "mid": v(-27.53, 31.78) * mm, "end": v(-25.55, 31.24) * mm});
            skPoint(sketch, "E353", {"position": v(-18.56, -13.52) * mm});
            skLineSegment(sketch, "E354", {"start": v(-18.56, -13.52) * mm, "end": v(-16.4, -13.5) * mm});
            skArc(sketch, "E355", {"start": v(-31.1, 3.06) * mm, "mid": v(-33.12, 3.3) * mm, "end": v(-35.09, 3.82) * mm});
            skLineSegment(sketch, "E356", {"start": v(-18.57, 13.52) * mm, "end": v(-16.35, 13.53) * mm});
            skLineSegment(sketch, "E357", {"start": v(-16.35, 13.53) * mm, "end": v(-16.35, 13.53) * mm});
            skPoint(sketch, "E358", {"position": v(-42.06, 12) * mm});
            skPoint(sketch, "E359", {"position": v(-43.71, 12) * mm});
            skLineSegment(sketch, "E360", {"start": v(-43.71, 12) * mm, "end": v(-42.06, 12) * mm});
            skPoint(sketch, "E361", {"position": v(-30.31, 17.5) * mm});
            skArc(sketch, "E362", {"start": v(-43.71, 12) * mm, "mid": v(-43.01, 10.53) * mm, "end": v(-42.15, 9.15) * mm});
            skLineSegment(sketch, "E363", {"start": v(-42.06, 12) * mm, "end": v(-42.15, 9.15) * mm});
            skPoint(sketch, "E364", {"position": v(30.2, 0) * mm});
            skPoint(sketch, "E365", {"position": v(26.32, 0) * mm});
            skPoint(sketch, "E366", {"position": v(33.98, 0) * mm});
            skPoint(sketch, "E367", {"position": v(30.3, -19.07) * mm});
            skLineSegment(sketch, "E368", {"start": v(30.3, -19.07) * mm, "end": v(30.3, 36.91) * mm});
            skLineSegment(sketch, "E369", {"start": v(30.3, -19.07) * mm, "end": v(30.32, -28.27) * mm});
            skPoint(sketch, "E370", {"position": v(30.3, 21.53) * mm});
            skPoint(sketch, "E371", {"position": v(30.27, 13.53) * mm});
            skPoint(sketch, "E372", {"position": v(30.27, 12.02) * mm});
            skPoint(sketch, "E373", {"position": v(30.3, 23.05) * mm});
            skPoint(sketch, "E374", {"position": v(31.06, 23.05) * mm});
            skPoint(sketch, "E375", {"position": v(35.06, 23.06) * mm});
            skPoint(sketch, "E376", {"position": v(25.56, 23.06) * mm});
            skPoint(sketch, "E377", {"position": v(30.3, 32.01) * mm});
            skPoint(sketch, "E378", {"position": v(24.06, 23.06) * mm});
            skPoint(sketch, "E379", {"position": v(35.07, 31.2) * mm});
            skPoint(sketch, "E380", {"position": v(36.56, 23.06) * mm});
            skPoint(sketch, "E381", {"position": v(29.56, 23.05) * mm});
            skPoint(sketch, "E382", {"position": v(20.06, 23.06) * mm});
            skPoint(sketch, "E383", {"position": v(18.56, 23.06) * mm});
            skPoint(sketch, "E384", {"position": v(40.56, 23.05) * mm});
            skPoint(sketch, "E385", {"position": v(42.06, 23.06) * mm});
            skPoint(sketch, "E386", {"position": v(16.35, -21.45) * mm});
            skPoint(sketch, "E387", {"position": v(16.9, -22.98) * mm});
            skPoint(sketch, "E388", {"position": v(18.56, -25.97) * mm});
            skPoint(sketch, "E389", {"position": v(18.56, -22.98) * mm});
            skPoint(sketch, "E390", {"position": v(20.06, -22.98) * mm});
            skPoint(sketch, "E391", {"position": v(24.05, -22.98) * mm});
            skPoint(sketch, "E392", {"position": v(25.56, -22.98) * mm});
            skPoint(sketch, "E393", {"position": v(20.06, -27.74) * mm});
            skPoint(sketch, "E394", {"position": v(24.05, -30.56) * mm});
            skPoint(sketch, "E395", {"position": v(25.56, -31.17) * mm});
            skPoint(sketch, "E396", {"position": v(29.54, -31.95) * mm});
            skPoint(sketch, "E397", {"position": v(31.05, -31.95) * mm});
            skPoint(sketch, "E398", {"position": v(35.05, -31.17) * mm});
            skPoint(sketch, "E399", {"position": v(36.56, -30.56) * mm});
            skPoint(sketch, "E400", {"position": v(24.05, -21.49) * mm});
            skPoint(sketch, "E401", {"position": v(25.56, -21.49) * mm});
            skPoint(sketch, "E402", {"position": v(30.31, -21.49) * mm});
            skPoint(sketch, "E403", {"position": v(30.32, -22.98) * mm});
            skPoint(sketch, "E404", {"position": v(31.05, -21.49) * mm});
            skPoint(sketch, "E405", {"position": v(31.05, -22.98) * mm});
            skPoint(sketch, "E406", {"position": v(29.54, -21.49) * mm});
            skPoint(sketch, "E407", {"position": v(29.54, -22.98) * mm});
            skPoint(sketch, "E408", {"position": v(35.05, -21.49) * mm});
            skPoint(sketch, "E409", {"position": v(35.05, -22.98) * mm});
            skPoint(sketch, "E410", {"position": v(36.56, -21.49) * mm});
            skPoint(sketch, "E411", {"position": v(36.56, -22.98) * mm});
            skPoint(sketch, "E412", {"position": v(40.55, -21.49) * mm});
            skPoint(sketch, "E413", {"position": v(40.55, -22.98) * mm});
            skPoint(sketch, "E414", {"position": v(42.05, -21.49) * mm});
            skPoint(sketch, "E415", {"position": v(42.03, -22.98) * mm});
            skPoint(sketch, "E416", {"position": v(44.25, -21.48) * mm});
            skPoint(sketch, "E417", {"position": v(43.71, -22.98) * mm});
            skPoint(sketch, "E418", {"position": v(40.54, -27.7) * mm});
            skPoint(sketch, "E419", {"position": v(42.03, -26) * mm});
            skPoint(sketch, "E420", {"position": v(16.4, -13.47) * mm});
            skPoint(sketch, "E421", {"position": v(18.54, -11.98) * mm});
            skPoint(sketch, "E422", {"position": v(18.56, -13.52) * mm});
            skPoint(sketch, "E423", {"position": v(20.04, -13.52) * mm});
            skPoint(sketch, "E424", {"position": v(20.04, -11.98) * mm});
            skPoint(sketch, "E425", {"position": v(24.05, -11.98) * mm});
            skPoint(sketch, "E426", {"position": v(24.05, -13.52) * mm});
            skPoint(sketch, "E427", {"position": v(25.57, -12.01) * mm});
            skPoint(sketch, "E428", {"position": v(25.57, -13.5) * mm});
            skPoint(sketch, "E429", {"position": v(29.54, -12.01) * mm});
            skPoint(sketch, "E430", {"position": v(29.54, -13.5) * mm});
            skPoint(sketch, "E431", {"position": v(31.06, -12.01) * mm});
            skPoint(sketch, "E432", {"position": v(31.06, -13.5) * mm});
            skPoint(sketch, "E433", {"position": v(35.08, -12.01) * mm});
            skPoint(sketch, "E434", {"position": v(35.08, -13.5) * mm});
            skPoint(sketch, "E435", {"position": v(36.54, -12.01) * mm});
            skPoint(sketch, "E436", {"position": v(36.54, -13.5) * mm});
            skPoint(sketch, "E437", {"position": v(40.56, -12.01) * mm});
            skPoint(sketch, "E438", {"position": v(40.55, -13.5) * mm});
            skPoint(sketch, "E439", {"position": v(42.05, -13.5) * mm});
            skPoint(sketch, "E440", {"position": v(44.24, -13.5) * mm});
            skPoint(sketch, "E441", {"position": v(42.06, -12.02) * mm});
            skPoint(sketch, "E442", {"position": v(43.72, -12.02) * mm});
            skPoint(sketch, "E443", {"position": v(16.9, -12.01) * mm});
            skPoint(sketch, "E444", {"position": v(20.07, -7.27) * mm});
            skPoint(sketch, "E445", {"position": v(24.05, -4.44) * mm});
            skPoint(sketch, "E446", {"position": v(25.6, -3.8) * mm});
            skPoint(sketch, "E447", {"position": v(29.57, -3.04) * mm});
            skPoint(sketch, "E448", {"position": v(31.07, -3.04) * mm});
            skPoint(sketch, "E449", {"position": v(35.06, -3.8) * mm});
            skPoint(sketch, "E450", {"position": v(36.56, -4.41) * mm});
            skPoint(sketch, "E451", {"position": v(40.57, -7.25) * mm});
            skPoint(sketch, "E452", {"position": v(42.06, -9.01) * mm});
            skPoint(sketch, "E453", {"position": v(30.3, -17.46) * mm});
            skPoint(sketch, "E454", {"position": v(18.57, -21.5) * mm});
            skPoint(sketch, "E455", {"position": v(20.04, -21.5) * mm});
            skLineSegment(sketch, "E456", {"start": v(20.04, -11.98) * mm, "end": v(24.05, -11.98) * mm});
            skLineSegment(sketch, "E457", {"start": v(25.57, -12.01) * mm, "end": v(29.54, -12.01) * mm});
            skLineSegment(sketch, "E458", {"start": v(16.9, -12.01) * mm, "end": v(18.54, -11.98) * mm});
            skLineSegment(sketch, "E459", {"start": v(16.4, -13.47) * mm, "end": v(18.56, -13.52) * mm});
            skLineSegment(sketch, "E460", {"start": v(20.04, -13.52) * mm, "end": v(24.05, -13.52) * mm});
            skLineSegment(sketch, "E461", {"start": v(25.57, -13.5) * mm, "end": v(29.54, -13.5) * mm});
            skLineSegment(sketch, "E462", {"start": v(16.35, -21.45) * mm, "end": v(18.57, -21.5) * mm});
            skLineSegment(sketch, "E463", {"start": v(20.04, -21.5) * mm, "end": v(24.05, -21.49) * mm});
            skLineSegment(sketch, "E464", {"start": v(25.56, -21.49) * mm, "end": v(29.54, -21.49) * mm});
            skLineSegment(sketch, "E465", {"start": v(16.9, -22.98) * mm, "end": v(18.56, -22.98) * mm});
            skLineSegment(sketch, "E466", {"start": v(20.06, -22.98) * mm, "end": v(24.05, -22.98) * mm});
            skLineSegment(sketch, "E467", {"start": v(25.56, -22.98) * mm, "end": v(29.54, -22.98) * mm});
            skLineSegment(sketch, "E468", {"start": v(18.56, -13.52) * mm, "end": v(18.57, -21.5) * mm});
            skLineSegment(sketch, "E469", {"start": v(20.04, -13.52) * mm, "end": v(20.04, -21.5) * mm});
            skLineSegment(sketch, "E470", {"start": v(24.05, -13.52) * mm, "end": v(24.05, -21.49) * mm});
            skLineSegment(sketch, "E471", {"start": v(25.57, -13.5) * mm, "end": v(25.56, -21.49) * mm});
            skLineSegment(sketch, "E472", {"start": v(29.54, -13.5) * mm, "end": v(29.54, -21.49) * mm});
            skLineSegment(sketch, "E473", {"start": v(31.06, -13.5) * mm, "end": v(31.05, -21.49) * mm});
            skArc(sketch, "E474", {"start": v(16.4, -13.47) * mm, "mid": v(15.85, -17.46) * mm, "end": v(16.4, -21.45) * mm});
            skPoint(sketch, "E475", {"position": v(18.56, -9.01) * mm});
            skLineSegment(sketch, "E476", {"start": v(18.56, -9.01) * mm, "end": v(18.54, -11.98) * mm});
            skLineSegment(sketch, "E477", {"start": v(20.07, -7.27) * mm, "end": v(20.04, -11.98) * mm});
            skLineSegment(sketch, "E478", {"start": v(24.05, -4.44) * mm, "end": v(24.05, -11.98) * mm});
            skLineSegment(sketch, "E479", {"start": v(25.6, -3.8) * mm, "end": v(25.57, -12.01) * mm});
            skLineSegment(sketch, "E480", {"start": v(29.57, -3.04) * mm, "end": v(29.54, -12.01) * mm});
            skLineSegment(sketch, "E481", {"start": v(31.07, -3.04) * mm, "end": v(31.06, -12.01) * mm});
            skArc(sketch, "E482", {"start": v(16.9, -12.01) * mm, "mid": v(17.64, -10.47) * mm, "end": v(18.56, -9.01) * mm});
            skArc(sketch, "E483", {"start": v(20.07, -7.27) * mm, "mid": v(21.94, -5.69) * mm, "end": v(24.05, -4.44) * mm});
            skArc(sketch, "E484", {"start": v(25.6, -3.8) * mm, "mid": v(27.56, -3.28) * mm, "end": v(29.57, -3.04) * mm});
            skLineSegment(sketch, "E485", {"start": v(31.06, -12.01) * mm, "end": v(35.08, -12.01) * mm});
            skLineSegment(sketch, "E486", {"start": v(36.54, -12.01) * mm, "end": v(40.56, -12.01) * mm});
            skLineSegment(sketch, "E487", {"start": v(42.06, -12.02) * mm, "end": v(43.72, -12.02) * mm});
            skLineSegment(sketch, "E488", {"start": v(31.06, -13.5) * mm, "end": v(35.08, -13.5) * mm});
            skLineSegment(sketch, "E489", {"start": v(36.54, -13.5) * mm, "end": v(40.55, -13.5) * mm});
            skLineSegment(sketch, "E490", {"start": v(42.05, -13.5) * mm, "end": v(44.24, -13.5) * mm});
            skLineSegment(sketch, "E491", {"start": v(31.05, -21.49) * mm, "end": v(35.05, -21.49) * mm});
            skLineSegment(sketch, "E492", {"start": v(36.56, -21.49) * mm, "end": v(40.55, -21.49) * mm});
            skLineSegment(sketch, "E493", {"start": v(42.05, -21.49) * mm, "end": v(44.25, -21.48) * mm});
            skLineSegment(sketch, "E494", {"start": v(31.05, -22.98) * mm, "end": v(35.05, -22.98) * mm});
            skLineSegment(sketch, "E495", {"start": v(36.56, -22.98) * mm, "end": v(40.55, -22.98) * mm});
            skLineSegment(sketch, "E496", {"start": v(42.03, -22.98) * mm, "end": v(43.71, -22.98) * mm});
            skLineSegment(sketch, "E497", {"start": v(35.08, -13.5) * mm, "end": v(35.05, -21.49) * mm});
            skLineSegment(sketch, "E498", {"start": v(36.54, -13.5) * mm, "end": v(36.56, -21.49) * mm});
            skLineSegment(sketch, "E499", {"start": v(40.55, -13.5) * mm, "end": v(40.55, -21.49) * mm});
            skLineSegment(sketch, "E500", {"start": v(42.05, -13.5) * mm, "end": v(42.05, -21.49) * mm});
            skArc(sketch, "E501", {"start": v(44.24, -13.5) * mm, "mid": v(44.8, -17.49) * mm, "end": v(44.23, -21.48) * mm});
            skLineSegment(sketch, "E502", {"start": v(18.56, -22.98) * mm, "end": v(18.56, -25.97) * mm});
            skLineSegment(sketch, "E503", {"start": v(20.06, -22.98) * mm, "end": v(20.06, -27.74) * mm});
            skLineSegment(sketch, "E504", {"start": v(24.05, -22.98) * mm, "end": v(24.05, -30.56) * mm});
            skLineSegment(sketch, "E505", {"start": v(25.56, -22.98) * mm, "end": v(25.56, -31.17) * mm});
            skLineSegment(sketch, "E506", {"start": v(29.54, -22.98) * mm, "end": v(29.54, -31.95) * mm});
            skLineSegment(sketch, "E507", {"start": v(31.05, -22.98) * mm, "end": v(31.05, -31.95) * mm});
            skLineSegment(sketch, "E508", {"start": v(35.05, -22.98) * mm, "end": v(35.05, -31.17) * mm});
            skLineSegment(sketch, "E509", {"start": v(36.56, -22.98) * mm, "end": v(36.56, -30.56) * mm});
            skLineSegment(sketch, "E510", {"start": v(40.55, -22.98) * mm, "end": v(40.54, -27.7) * mm});
            skLineSegment(sketch, "E511", {"start": v(42.03, -22.98) * mm, "end": v(42.03, -26) * mm});
            skArc(sketch, "E512", {"start": v(43.71, -22.98) * mm, "mid": v(42.96, -24.54) * mm, "end": v(42.03, -26) * mm});
            skArc(sketch, "E513", {"start": v(40.54, -27.7) * mm, "mid": v(38.67, -29.28) * mm, "end": v(36.56, -30.52) * mm});
            skArc(sketch, "E514", {"start": v(35.05, -31.17) * mm, "mid": v(33.08, -31.7) * mm, "end": v(31.05, -31.95) * mm});
            skArc(sketch, "E515", {"start": v(29.54, -31.95) * mm, "mid": v(38.72, -29.28) * mm, "end": v(44.25, -21.48) * mm});
            skArc(sketch, "E516", {"start": v(16.9, -22.98) * mm, "mid": v(17.64, -24.52) * mm, "end": v(18.56, -25.97) * mm});
            skArc(sketch, "E517", {"start": v(20.06, -27.74) * mm, "mid": v(21.94, -29.32) * mm, "end": v(24.05, -30.56) * mm});
            skArc(sketch, "E518", {"start": v(25.56, -31.17) * mm, "mid": v(27.52, -31.7) * mm, "end": v(29.54, -31.95) * mm});
            skLineSegment(sketch, "E519", {"start": v(35.06, -3.8) * mm, "end": v(35.08, -12.01) * mm});
            skLineSegment(sketch, "E520", {"start": v(36.56, -4.41) * mm, "end": v(36.54, -12.01) * mm});
            skLineSegment(sketch, "E521", {"start": v(40.57, -7.25) * mm, "end": v(40.56, -12.01) * mm});
            skLineSegment(sketch, "E522", {"start": v(42.06, -9.01) * mm, "end": v(42.06, -12.02) * mm});
            skArc(sketch, "E523", {"start": v(31.07, -3.04) * mm, "mid": v(33.1, -3.29) * mm, "end": v(35.06, -3.82) * mm});
            skArc(sketch, "E524", {"start": v(36.56, -4.41) * mm, "mid": v(38.68, -5.66) * mm, "end": v(40.57, -7.26) * mm});
            skArc(sketch, "E525", {"start": v(42.06, -9.01) * mm, "mid": v(42.98, -10.46) * mm, "end": v(43.72, -12.02) * mm});
            skPoint(sketch, "E526", {"position": v(16.9, 12.05) * mm});
            skPoint(sketch, "E527", {"position": v(16.37, 13.52) * mm});
            skPoint(sketch, "E528", {"position": v(18.55, 13.5) * mm});
            skPoint(sketch, "E529", {"position": v(18.55, 12.05) * mm});
            skPoint(sketch, "E530", {"position": v(20.07, 12.05) * mm});
            skPoint(sketch, "E531", {"position": v(20.07, 13.5) * mm});
            skPoint(sketch, "E532", {"position": v(18.55, 9.04) * mm});
            skPoint(sketch, "E533", {"position": v(20.06, 7.25) * mm});
            skPoint(sketch, "E534", {"position": v(24.06, 4.42) * mm});
            skPoint(sketch, "E535", {"position": v(25.56, 3.83) * mm});
            skPoint(sketch, "E536", {"position": v(29.56, 3.05) * mm});
            skPoint(sketch, "E537", {"position": v(31.06, 3.06) * mm});
            skPoint(sketch, "E538", {"position": v(35.06, 3.81) * mm});
            skPoint(sketch, "E539", {"position": v(36.56, 4.42) * mm});
            skPoint(sketch, "E540", {"position": v(40.56, 7.24) * mm});
            skPoint(sketch, "E541", {"position": v(42.06, 9.03) * mm});
            skPoint(sketch, "E542", {"position": v(42.05, 12.05) * mm});
            skPoint(sketch, "E543", {"position": v(40.56, 12.05) * mm});
            skPoint(sketch, "E544", {"position": v(36.53, 12.05) * mm});
            skPoint(sketch, "E545", {"position": v(35.04, 12.05) * mm});
            skPoint(sketch, "E546", {"position": v(43.73, 12.05) * mm});
            skPoint(sketch, "E547", {"position": v(44.23, 13.49) * mm});
            skPoint(sketch, "E548", {"position": v(42.04, 13.47) * mm});
            skPoint(sketch, "E549", {"position": v(40.54, 13.47) * mm});
            skPoint(sketch, "E550", {"position": v(36.53, 13.47) * mm});
            skPoint(sketch, "E551", {"position": v(35.03, 13.47) * mm});
            skPoint(sketch, "E552", {"position": v(31.07, 13.47) * mm});
            skPoint(sketch, "E553", {"position": v(31.05, 12.04) * mm});
            skPoint(sketch, "E554", {"position": v(24.06, 13.5) * mm});
            skPoint(sketch, "E555", {"position": v(25.56, 13.5) * mm});
            skPoint(sketch, "E556", {"position": v(29.57, 13.5) * mm});
            skPoint(sketch, "E557", {"position": v(24.06, 12.07) * mm});
            skPoint(sketch, "E558", {"position": v(25.56, 12.07) * mm});
            skPoint(sketch, "E559", {"position": v(29.55, 12.06) * mm});
            skPoint(sketch, "E560", {"position": v(16.38, 21.5) * mm});
            skPoint(sketch, "E561", {"position": v(18.56, 21.5) * mm});
            skPoint(sketch, "E562", {"position": v(20.06, 21.57) * mm});
            skPoint(sketch, "E563", {"position": v(24.06, 21.57) * mm});
            skPoint(sketch, "E564", {"position": v(25.56, 21.57) * mm});
            skPoint(sketch, "E565", {"position": v(29.56, 21.57) * mm});
            skPoint(sketch, "E566", {"position": v(31.06, 21.57) * mm});
            skPoint(sketch, "E567", {"position": v(35.04, 21.57) * mm});
            skPoint(sketch, "E568", {"position": v(36.55, 21.57) * mm});
            skPoint(sketch, "E569", {"position": v(40.55, 21.57) * mm});
            skPoint(sketch, "E570", {"position": v(42.05, 21.57) * mm});
            skPoint(sketch, "E571", {"position": v(44.23, 21.57) * mm});
            skPoint(sketch, "E572", {"position": v(43.68, 23.07) * mm});
            skPoint(sketch, "E573", {"position": v(18.55, 25.97) * mm});
            skPoint(sketch, "E574", {"position": v(20.07, 27.77) * mm});
            skPoint(sketch, "E575", {"position": v(24.06, 30.59) * mm});
            skPoint(sketch, "E576", {"position": v(29.56, 31.98) * mm});
            skPoint(sketch, "E577", {"position": v(25.56, 31.2) * mm});
            skPoint(sketch, "E578", {"position": v(30.98, 31.98) * mm});
            skPoint(sketch, "E579", {"position": v(36.57, 30.59) * mm});
            skPoint(sketch, "E580", {"position": v(40.56, 27.77) * mm});
            skPoint(sketch, "E581", {"position": v(42.07, 25.97) * mm});
            skLineSegment(sketch, "E582", {"start": v(20.06, 23.06) * mm, "end": v(24.06, 23.06) * mm});
            skLineSegment(sketch, "E583", {"start": v(25.56, 23.06) * mm, "end": v(29.56, 23.05) * mm});
            skLineSegment(sketch, "E584", {"start": v(16.38, 21.5) * mm, "end": v(18.56, 21.5) * mm});
            skLineSegment(sketch, "E585", {"start": v(20.06, 21.57) * mm, "end": v(24.06, 21.57) * mm});
            skLineSegment(sketch, "E586", {"start": v(25.56, 21.57) * mm, "end": v(29.56, 21.57) * mm});
            skLineSegment(sketch, "E587", {"start": v(31.06, 23.05) * mm, "end": v(35.06, 23.06) * mm});
            skLineSegment(sketch, "E588", {"start": v(36.56, 23.06) * mm, "end": v(40.56, 23.05) * mm});
            skLineSegment(sketch, "E589", {"start": v(31.06, 21.57) * mm, "end": v(35.04, 21.57) * mm});
            skLineSegment(sketch, "E590", {"start": v(36.55, 21.57) * mm, "end": v(40.55, 21.57) * mm});
            skLineSegment(sketch, "E591", {"start": v(18.55, 25.97) * mm, "end": v(18.56, 23.06) * mm});
            skLineSegment(sketch, "E592", {"start": v(20.07, 27.77) * mm, "end": v(20.06, 23.06) * mm});
            skLineSegment(sketch, "E593", {"start": v(24.06, 30.59) * mm, "end": v(24.06, 23.06) * mm});
            skLineSegment(sketch, "E594", {"start": v(25.56, 31.2) * mm, "end": v(25.56, 23.06) * mm});
            skLineSegment(sketch, "E595", {"start": v(29.56, 31.98) * mm, "end": v(29.56, 23.05) * mm});
            skLineSegment(sketch, "E596", {"start": v(30.98, 31.98) * mm, "end": v(31.06, 23.05) * mm});
            skLineSegment(sketch, "E597", {"start": v(35.07, 31.2) * mm, "end": v(35.06, 23.06) * mm});
            skLineSegment(sketch, "E598", {"start": v(36.57, 30.59) * mm, "end": v(36.56, 23.06) * mm});
            skLineSegment(sketch, "E599", {"start": v(40.56, 27.77) * mm, "end": v(40.56, 23.05) * mm});
            skLineSegment(sketch, "E600", {"start": v(42.07, 25.97) * mm, "end": v(42.06, 23.06) * mm});
            skLineSegment(sketch, "E601", {"start": v(42.05, 21.57) * mm, "end": v(44.23, 21.57) * mm});
            skLineSegment(sketch, "E602", {"start": v(16.37, 13.52) * mm, "end": v(18.55, 13.5) * mm});
            skLineSegment(sketch, "E603", {"start": v(18.56, 21.5) * mm, "end": v(18.55, 13.5) * mm});
            skLineSegment(sketch, "E604", {"start": v(20.06, 21.57) * mm, "end": v(20.07, 13.5) * mm});
            skLineSegment(sketch, "E605", {"start": v(24.06, 13.5) * mm, "end": v(24.06, 21.57) * mm});
            skLineSegment(sketch, "E606", {"start": v(25.56, 21.57) * mm, "end": v(25.56, 13.5) * mm});
            skLineSegment(sketch, "E607", {"start": v(29.57, 13.5) * mm, "end": v(29.56, 21.57) * mm});
            skLineSegment(sketch, "E608", {"start": v(31.06, 21.57) * mm, "end": v(31.07, 13.47) * mm});
            skLineSegment(sketch, "E609", {"start": v(35.03, 13.47) * mm, "end": v(35.04, 21.57) * mm});
            skLineSegment(sketch, "E610", {"start": v(36.55, 21.57) * mm, "end": v(36.53, 13.47) * mm});
            skLineSegment(sketch, "E611", {"start": v(40.54, 13.47) * mm, "end": v(40.55, 21.57) * mm});
            skLineSegment(sketch, "E612", {"start": v(42.05, 21.57) * mm, "end": v(42.04, 13.47) * mm});
            skLineSegment(sketch, "E613", {"start": v(16.9, 12.05) * mm, "end": v(18.55, 12.05) * mm});
            skLineSegment(sketch, "E614", {"start": v(18.55, 12.05) * mm, "end": v(18.55, 9.04) * mm});
            skLineSegment(sketch, "E615", {"start": v(20.07, 12.05) * mm, "end": v(24.06, 12.07) * mm});
            skLineSegment(sketch, "E616", {"start": v(25.56, 12.07) * mm, "end": v(29.55, 12.06) * mm});
            skLineSegment(sketch, "E617", {"start": v(31.05, 12.04) * mm, "end": v(35.04, 12.05) * mm});
            skLineSegment(sketch, "E618", {"start": v(36.53, 12.05) * mm, "end": v(40.56, 12.05) * mm});
            skLineSegment(sketch, "E619", {"start": v(42.05, 12.05) * mm, "end": v(43.73, 12.05) * mm});
            skLineSegment(sketch, "E620", {"start": v(42.05, 12.05) * mm, "end": v(42.06, 9.03) * mm});
            skLineSegment(sketch, "E621", {"start": v(20.07, 12.05) * mm, "end": v(20.06, 7.25) * mm});
            skLineSegment(sketch, "E622", {"start": v(24.06, 12.07) * mm, "end": v(24.06, 4.42) * mm});
            skLineSegment(sketch, "E623", {"start": v(25.56, 12.07) * mm, "end": v(25.56, 3.83) * mm});
            skLineSegment(sketch, "E624", {"start": v(29.55, 12.06) * mm, "end": v(29.56, 3.05) * mm});
            skLineSegment(sketch, "E625", {"start": v(31.05, 12.04) * mm, "end": v(31.06, 3.06) * mm});
            skLineSegment(sketch, "E626", {"start": v(35.04, 12.05) * mm, "end": v(35.06, 3.81) * mm});
            skLineSegment(sketch, "E627", {"start": v(36.53, 12.05) * mm, "end": v(36.56, 4.42) * mm});
            skLineSegment(sketch, "E628", {"start": v(40.56, 12.05) * mm, "end": v(40.56, 7.24) * mm});
            skArc(sketch, "E629", {"start": v(20.07, 27.77) * mm, "mid": v(21.95, 29.35) * mm, "end": v(24.06, 30.59) * mm});
            skArc(sketch, "E630", {"start": v(25.56, 31.2) * mm, "mid": v(27.53, 31.72) * mm, "end": v(29.56, 31.97) * mm});
            skArc(sketch, "E631", {"start": v(30.98, 31.98) * mm, "mid": v(33.05, 31.73) * mm, "end": v(35.07, 31.2) * mm});
            skArc(sketch, "E632", {"start": v(36.57, 30.59) * mm, "mid": v(38.68, 29.35) * mm, "end": v(40.56, 27.76) * mm});
            skArc(sketch, "E633", {"start": v(42.07, 25.97) * mm, "mid": v(42.96, 24.57) * mm, "end": v(43.68, 23.07) * mm});
            skArc(sketch, "E634", {"start": v(16.38, 21.5) * mm, "mid": v(15.82, 17.51) * mm, "end": v(16.39, 13.52) * mm});
            skArc(sketch, "E635", {"start": v(44.23, 21.57) * mm, "mid": v(44.8, 17.53) * mm, "end": v(44.23, 13.49) * mm});
            skArc(sketch, "E636", {"start": v(43.73, 12.05) * mm, "mid": v(42.98, 10.5) * mm, "end": v(42.06, 9.04) * mm});
            skArc(sketch, "E637", {"start": v(40.56, 7.24) * mm, "mid": v(38.68, 5.66) * mm, "end": v(36.56, 4.42) * mm});
            skArc(sketch, "E638", {"start": v(16.9, 12.05) * mm, "mid": v(17.64, 10.5) * mm, "end": v(18.55, 9.06) * mm});
            skArc(sketch, "E639", {"start": v(20.06, 7.25) * mm, "mid": v(21.94, 5.66) * mm, "end": v(24.06, 4.42) * mm});
            skArc(sketch, "E640", {"start": v(25.56, 3.83) * mm, "mid": v(27.53, 3.3) * mm, "end": v(29.56, 3.05) * mm});
            skArc(sketch, "E641", {"start": v(31.06, 3.06) * mm, "mid": v(33.09, 3.31) * mm, "end": v(35.06, 3.84) * mm});
            skLineSegment(sketch, "E642", {"start": v(20.07, 13.5) * mm, "end": v(24.06, 13.5) * mm});
            skLineSegment(sketch, "E643", {"start": v(25.56, 13.5) * mm, "end": v(29.57, 13.5) * mm});
            skLineSegment(sketch, "E644", {"start": v(31.07, 13.47) * mm, "end": v(35.03, 13.47) * mm});
            skLineSegment(sketch, "E645", {"start": v(36.53, 13.47) * mm, "end": v(40.54, 13.47) * mm});
            skLineSegment(sketch, "E646", {"start": v(42.04, 13.47) * mm, "end": v(44.23, 13.49) * mm});
            skLineSegment(sketch, "E647", {"start": v(42.06, 23.06) * mm, "end": v(43.68, 23.07) * mm});
            skPoint(sketch, "E648", {"position": v(16.94, 23.06) * mm});
            skLineSegment(sketch, "E649", {"start": v(16.94, 23.06) * mm, "end": v(18.56, 23.06) * mm});
            skArc(sketch, "E650", {"start": v(16.94, 23.06) * mm, "mid": v(17.66, 24.56) * mm, "end": v(18.55, 25.96) * mm});
            skSolve(sketch);
        }
        {
            var Q0;
            Q0=makeQuery(id+"F1.imprint","IMPRINT",FACE,{"disambiguationData":[TD([[makeQuery(id+"F1.imprint","IMPRINT",EDGE,{"derivedFrom":sQuery(id+"F1.wireOp",EDGE,"E143.bottom")}),1.0]])]});
            extrude(context, id + "F2", {"entities" : qUnion([Q0]), "depth" : 4 * mm, "offsetDistance" : 25 * mm});
        }
        {
            var Q0;
            {var subQ0=sQuery(id+"F0.wireOp",EDGE,"E20");var subQ1=sQuery(id+"F0.wireOp",EDGE,"QIJiGY5w-lFCi-xx9X-rp0q-5GBFziIUs7mU");var subQ2=makeQuery(id+"F0.imprint","INTERSECT",VERTEX,{"disambiguationData":[OD(0.0)],"derivedFrom":[subQ1,subQ0]});Q0=makeQuery(id+"F0.imprint","IMPRINT",FACE,{"disambiguationData":[TD([[makeQuery(id+"F0.imprint","IMPRINT",EDGE,{"disambiguationData":[TD([[subQ2,-1.0]])],"derivedFrom":subQ1}),-1.0]])]});}
            var Q1;
            {var subQ0=sQuery(id+"F0.wireOp",EDGE,"E21");var subQ1=sQuery(id+"F0.wireOp",EDGE,"E5");var subQ2=makeQuery(id+"F0.imprint","INTERSECT",VERTEX,{"disambiguationData":[OD(0.0)],"derivedFrom":[subQ1,subQ0]});Q1=makeQuery(id+"F0.imprint","IMPRINT",FACE,{"disambiguationData":[TD([[makeQuery(id+"F0.imprint","IMPRINT",EDGE,{"disambiguationData":[TD([[subQ2,-1.0]])],"derivedFrom":subQ1}),1.0]])]});}
            var Q2;
            {var subQ0=sQuery(id+"F0.wireOp",EDGE,"E21");var subQ1=sQuery(id+"F0.wireOp",EDGE,"E5");var subQ2=makeQuery(id+"F0.imprint","INTERSECT",VERTEX,{"disambiguationData":[OD(0.0)],"derivedFrom":[subQ1,subQ0]});Q2=makeQuery(id+"F0.imprint","IMPRINT",FACE,{"disambiguationData":[TD([[makeQuery(id+"F0.imprint","IMPRINT",EDGE,{"disambiguationData":[TD([[subQ2,-1.0]])],"derivedFrom":subQ1}),-1.0]])]});}
            var Q3;
            {var subQ0=sQuery(id+"F0.wireOp",EDGE,"E22");var subQ1=sQuery(id+"F0.wireOp",EDGE,"b7w3sZkz-h2S3-PTXa-qy05-PL4N3AHQH3GV");var subQ2=makeQuery(id+"F0.imprint","INTERSECT",VERTEX,{"disambiguationData":[OD(0.0)],"derivedFrom":[subQ1,subQ0]});Q3=makeQuery(id+"F0.imprint","IMPRINT",FACE,{"disambiguationData":[TD([[makeQuery(id+"F0.imprint","IMPRINT",EDGE,{"disambiguationData":[TD([[subQ2,-1.0]])],"derivedFrom":subQ1}),-1.0]])]});}
            var Q4;
            {var subQ0=sQuery(id+"F0.wireOp",EDGE,"E5");var subQ1=sQuery(id+"F0.wireOp",EDGE,"b7w3sZkz-h2S3-PTXa-qy05-PL4N3AHQH3GV");var subQ2=makeQuery(id+"F0.imprint","INTERSECT",VERTEX,{"disambiguationData":[OD(0.0)],"derivedFrom":[subQ1,subQ0]});Q4=makeQuery(id+"F0.imprint","IMPRINT",FACE,{"disambiguationData":[TD([[makeQuery(id+"F0.imprint","IMPRINT",EDGE,{"disambiguationData":[TD([[subQ2,-1.0]])],"derivedFrom":subQ1}),-1.0]])]});}
            var Q5;
            {var subQ0=sQuery(id+"F0.wireOp",EDGE,"E5");var subQ1=sQuery(id+"F0.wireOp",EDGE,"b7w3sZkz-h2S3-PTXa-qy05-PL4N3AHQH3GV");var subQ2=makeQuery(id+"F0.imprint","INTERSECT",VERTEX,{"disambiguationData":[OD(0.0)],"derivedFrom":[subQ1,subQ0]});Q5=makeQuery(id+"F0.imprint","IMPRINT",FACE,{"disambiguationData":[TD([[makeQuery(id+"F0.imprint","IMPRINT",EDGE,{"disambiguationData":[TD([[subQ2,-1.0]])],"derivedFrom":subQ1}),1.0]])]});}
            var Q6;
            {var subQ0=sQuery(id+"F0.wireOp",EDGE,"E22");var subQ1=sQuery(id+"F0.wireOp",EDGE,"b7w3sZkz-h2S3-PTXa-qy05-PL4N3AHQH3GV");var subQ2=makeQuery(id+"F0.imprint","INTERSECT",VERTEX,{"disambiguationData":[OD(0.0)],"derivedFrom":[subQ1,subQ0]});Q6=makeQuery(id+"F0.imprint","IMPRINT",FACE,{"disambiguationData":[TD([[makeQuery(id+"F0.imprint","IMPRINT",EDGE,{"disambiguationData":[TD([[subQ2,-1.0]])],"derivedFrom":subQ1}),1.0]])]});}
            var Q7;
            {var subQ0=sQuery(id+"F0.wireOp",EDGE,"E23");var subQ1=sQuery(id+"F0.wireOp",EDGE,"QIJiGY5w-lFCi-xx9X-rp0q-5GBFziIUs7mU");var subQ2=makeQuery(id+"F0.imprint","INTERSECT",VERTEX,{"disambiguationData":[OD(0.0)],"derivedFrom":[subQ1,subQ0]});Q7=makeQuery(id+"F0.imprint","IMPRINT",FACE,{"disambiguationData":[TD([[makeQuery(id+"F0.imprint","IMPRINT",EDGE,{"disambiguationData":[TD([[subQ2,-1.0]])],"derivedFrom":subQ1}),1.0]])]});}
            var Q8;
            {var subQ0=sQuery(id+"F0.wireOp",EDGE,"E5");var subQ1=sQuery(id+"F0.wireOp",EDGE,"QIJiGY5w-lFCi-xx9X-rp0q-5GBFziIUs7mU");var subQ2=makeQuery(id+"F0.imprint","INTERSECT",VERTEX,{"disambiguationData":[OD(1.0)],"derivedFrom":[subQ1,subQ0]});Q8=makeQuery(id+"F0.imprint","IMPRINT",FACE,{"disambiguationData":[TD([[makeQuery(id+"F0.imprint","IMPRINT",EDGE,{"disambiguationData":[TD([[subQ2,-1.0]])],"derivedFrom":subQ1}),1.0]])]});}
            var Q9;
            {var subQ0=sQuery(id+"F0.wireOp",EDGE,"E5");var subQ1=sQuery(id+"F0.wireOp",EDGE,"QIJiGY5w-lFCi-xx9X-rp0q-5GBFziIUs7mU");var subQ2=makeQuery(id+"F0.imprint","INTERSECT",VERTEX,{"disambiguationData":[OD(1.0)],"derivedFrom":[subQ1,subQ0]});Q9=makeQuery(id+"F0.imprint","IMPRINT",FACE,{"disambiguationData":[TD([[makeQuery(id+"F0.imprint","IMPRINT",EDGE,{"disambiguationData":[TD([[subQ2,-1.0]])],"derivedFrom":subQ1}),-1.0]])]});}
            var Q10;
            {var subQ0=sQuery(id+"F0.wireOp",EDGE,"E23");var subQ1=sQuery(id+"F0.wireOp",EDGE,"QIJiGY5w-lFCi-xx9X-rp0q-5GBFziIUs7mU");var subQ2=makeQuery(id+"F0.imprint","INTERSECT",VERTEX,{"disambiguationData":[OD(0.0)],"derivedFrom":[subQ1,subQ0]});Q10=makeQuery(id+"F0.imprint","IMPRINT",FACE,{"disambiguationData":[TD([[makeQuery(id+"F0.imprint","IMPRINT",EDGE,{"disambiguationData":[TD([[subQ2,-1.0]])],"derivedFrom":subQ1}),-1.0]])]});}
            var Q11;
            {var subQ0=sQuery(id+"F0.wireOp",EDGE,"E24");var subQ1=sQuery(id+"F0.wireOp",EDGE,"E5");var subQ2=makeQuery(id+"F0.imprint","INTERSECT",VERTEX,{"disambiguationData":[OD(0.0)],"derivedFrom":[subQ1,subQ0]});Q11=makeQuery(id+"F0.imprint","IMPRINT",FACE,{"disambiguationData":[TD([[makeQuery(id+"F0.imprint","IMPRINT",EDGE,{"disambiguationData":[TD([[subQ2,-1.0]])],"derivedFrom":subQ1}),-1.0]])]});}
            var Q12;
            {var subQ0=sQuery(id+"F0.wireOp",EDGE,"E24");var subQ1=sQuery(id+"F0.wireOp",EDGE,"E5");var subQ2=makeQuery(id+"F0.imprint","INTERSECT",VERTEX,{"disambiguationData":[OD(0.0)],"derivedFrom":[subQ1,subQ0]});Q12=makeQuery(id+"F0.imprint","IMPRINT",FACE,{"disambiguationData":[TD([[makeQuery(id+"F0.imprint","IMPRINT",EDGE,{"disambiguationData":[TD([[subQ2,-1.0]])],"derivedFrom":subQ1}),1.0]])]});}
            var Q13;
            {var subQ0=sQuery(id+"F0.wireOp",EDGE,"E19");var subQ1=sQuery(id+"F0.wireOp",EDGE,"QIJiGY5w-lFCi-xx9X-rp0q-5GBFziIUs7mU");var subQ2=makeQuery(id+"F0.imprint","INTERSECT",VERTEX,{"disambiguationData":[OD(0.0)],"derivedFrom":[subQ1,subQ0]});Q13=makeQuery(id+"F0.imprint","IMPRINT",FACE,{"disambiguationData":[TD([[makeQuery(id+"F0.imprint","IMPRINT",EDGE,{"disambiguationData":[TD([[subQ2,-1.0]])],"derivedFrom":subQ1}),1.0]])]});}
            var Q14;
            {var subQ0=sQuery(id+"F0.wireOp",EDGE,"E19");var subQ1=sQuery(id+"F0.wireOp",EDGE,"QIJiGY5w-lFCi-xx9X-rp0q-5GBFziIUs7mU");var subQ2=makeQuery(id+"F0.imprint","INTERSECT",VERTEX,{"disambiguationData":[OD(0.0)],"derivedFrom":[subQ1,subQ0]});Q14=makeQuery(id+"F0.imprint","IMPRINT",FACE,{"disambiguationData":[TD([[makeQuery(id+"F0.imprint","IMPRINT",EDGE,{"disambiguationData":[TD([[subQ2,-1.0]])],"derivedFrom":subQ1}),-1.0]])]});}
            var Q15;
            {var subQ0=sQuery(id+"F0.wireOp",EDGE,"b7w3sZkz-h2S3-PTXa-qy05-PL4N3AHQH3GV");var subQ1=sQuery(id+"F0.wireOp",EDGE,"QIJiGY5w-lFCi-xx9X-rp0q-5GBFziIUs7mU");var subQ2=makeQuery(id+"F0.imprint","INTERSECT",VERTEX,{"derivedFrom":[subQ1,subQ0]});Q15=makeQuery(id+"F0.imprint","IMPRINT",FACE,{"disambiguationData":[TD([[makeQuery(id+"F0.imprint","IMPRINT",EDGE,{"disambiguationData":[TD([[subQ2,-1.0]])],"derivedFrom":subQ1}),-1.0]])]});}
            var Q16;
            {var subQ0=sQuery(id+"F0.wireOp",EDGE,"b7w3sZkz-h2S3-PTXa-qy05-PL4N3AHQH3GV");var subQ1=sQuery(id+"F0.wireOp",EDGE,"QIJiGY5w-lFCi-xx9X-rp0q-5GBFziIUs7mU");var subQ2=makeQuery(id+"F0.imprint","INTERSECT",VERTEX,{"derivedFrom":[subQ1,subQ0]});Q16=makeQuery(id+"F0.imprint","IMPRINT",FACE,{"disambiguationData":[TD([[makeQuery(id+"F0.imprint","IMPRINT",EDGE,{"disambiguationData":[TD([[subQ2,-1.0]])],"derivedFrom":subQ1}),1.0]])]});}
            var Q17;
            Q17=makeQuery(id+"F0.imprint","IMPRINT",FACE,{"disambiguationData":[TD([[makeQuery(id+"F0.imprint","IMPRINT",EDGE,{"derivedFrom":sQuery(id+"F0.wireOp",EDGE,"E28")}),-1.0]])]});
            var Q18;
            Q18=makeQuery(id+"F0.imprint","IMPRINT",FACE,{"disambiguationData":[TD([[makeQuery(id+"F0.imprint","IMPRINT",EDGE,{"derivedFrom":sQuery(id+"F0.wireOp",EDGE,"E37")}),1.0]])]});
            var Q19;
            Q19=makeQuery(id+"F0.imprint","IMPRINT",FACE,{"disambiguationData":[TD([[makeQuery(id+"F0.imprint","IMPRINT",EDGE,{"derivedFrom":sQuery(id+"F0.wireOp",EDGE,"E40")}),-1.0]])]});
            var Q20;
            Q20=makeQuery(id+"F0.imprint","IMPRINT",FACE,{"disambiguationData":[TD([[makeQuery(id+"F0.imprint","IMPRINT",EDGE,{"derivedFrom":sQuery(id+"F0.wireOp",EDGE,"E43")}),-1.0]])]});
            var Q21;
            Q21=makeQuery(id+"F0.imprint","IMPRINT",FACE,{"disambiguationData":[TD([[makeQuery(id+"F0.imprint","IMPRINT",EDGE,{"derivedFrom":sQuery(id+"F0.wireOp",EDGE,"E32")}),1.0]])]});
            var Q22;
            Q22=makeQuery(id+"F0.imprint","IMPRINT",FACE,{"disambiguationData":[TD([[makeQuery(id+"F0.imprint","IMPRINT",EDGE,{"derivedFrom":sQuery(id+"F0.wireOp",EDGE,"E35")}),1.0]])]});
            var Q23;
            Q23=makeQuery(id+"F1.imprint","IMPRINT",FACE,{"disambiguationData":[TD([[makeQuery(id+"F1.imprint","IMPRINT",EDGE,{"derivedFrom":sQuery(id+"F1.wireOp",EDGE,"E601")}),-1.0]])]});
            var Q24;
            Q24=makeQuery(id+"F2.opExtrude","CAP_FACE",FACE,{"disambiguationData":[OSD([sQuery(id+"F1.wireOp",EDGE,"E74"),sQuery(id+"F1.wireOp",EDGE,"E143.bottom"),sQuery(id+"F1.wireOp",EDGE,"E143.right"),sQuery(id+"F1.wireOp",EDGE,"E144.bottom"),sQuery(id+"F1.wireOp",EDGE,"E144.left"),sQuery(id+"F1.wireOp",EDGE,"E144.right"),sQuery(id+"F1.wireOp",EDGE,"E145.left"),sQuery(id+"F1.wireOp",EDGE,"E145.right"),sQuery(id+"F1.wireOp",EDGE,"E146.left"),sQuery(id+"F1.wireOp",EDGE,"E146.right"),sQuery(id+"F1.wireOp",EDGE,"E142.left"),sQuery(id+"F1.wireOp",EDGE,"E148.bottom"),sQuery(id+"F1.wireOp",EDGE,"E149.bottom"),sQuery(id+"F1.wireOp",EDGE,"E150"),sQuery(id+"F1.wireOp",EDGE,"E145.bottom"),sQuery(id+"F1.wireOp",EDGE,"E146.bottom"),sQuery(id+"F1.wireOp",EDGE,"E147.top"),sQuery(id+"F1.wireOp",EDGE,"E144.top"),sQuery(id+"F1.wireOp",EDGE,"E145.top"),sQuery(id+"F1.wireOp",EDGE,"E146.top"),sQuery(id+"F1.wireOp",EDGE,"E151"),sQuery(id+"F1.wireOp",EDGE,"E152"),sQuery(id+"F1.wireOp",EDGE,"E153"),sQuery(id+"F1.wireOp",EDGE,"E155"),sQuery(id+"F1.wireOp",EDGE,"E158"),sQuery(id+"F1.wireOp",EDGE,"E159"),sQuery(id+"F1.wireOp",EDGE,"E163"),sQuery(id+"F1.wireOp",EDGE,"E162"),sQuery(id+"F1.wireOp",EDGE,"E156"),sQuery(id+"F1.wireOp",EDGE,"E157"),sQuery(id+"F1.wireOp",EDGE,"E165"),sQuery(id+"F1.wireOp",EDGE,"E167"),sQuery(id+"F1.wireOp",EDGE,"E170"),sQuery(id+"F1.wireOp",EDGE,"E171"),sQuery(id+"F1.wireOp",EDGE,"E178"),sQuery(id+"F1.wireOp",EDGE,"E182"),sQuery(id+"F1.wireOp",EDGE,"E183"),sQuery(id+"F1.wireOp",EDGE,"E184"),sQuery(id+"F1.wireOp",EDGE,"E190"),sQuery(id+"F1.wireOp",EDGE,"E191"),sQuery(id+"F1.wireOp",EDGE,"E195"),sQuery(id+"F1.wireOp",EDGE,"E199"),sQuery(id+"F1.wireOp",EDGE,"E200"),sQuery(id+"F1.wireOp",EDGE,"E201"),sQuery(id+"F1.wireOp",EDGE,"E185"),sQuery(id+"F1.wireOp",EDGE,"E203"),sQuery(id+"F1.wireOp",EDGE,"E205"),sQuery(id+"F1.wireOp",EDGE,"E207"),sQuery(id+"F1.wireOp",EDGE,"E208"),sQuery(id+"F1.wireOp",EDGE,"E209"),sQuery(id+"F1.wireOp",EDGE,"E210"),sQuery(id+"F1.wireOp",EDGE,"E212"),sQuery(id+"F1.wireOp",EDGE,"E214"),sQuery(id+"F1.wireOp",EDGE,"E215"),sQuery(id+"F1.wireOp",EDGE,"E216"),sQuery(id+"F1.wireOp",EDGE,"E217"),sQuery(id+"F1.wireOp",EDGE,"E218"),sQuery(id+"F1.wireOp",EDGE,"E219"),sQuery(id+"F1.wireOp",EDGE,"E222"),sQuery(id+"F1.wireOp",EDGE,"E224"),sQuery(id+"F1.wireOp",EDGE,"E223"),sQuery(id+"F1.wireOp",EDGE,"E189"),sQuery(id+"F1.wireOp",EDGE,"E225"),sQuery(id+"F1.wireOp",EDGE,"E226"),sQuery(id+"F1.wireOp",EDGE,"E227"),sQuery(id+"F1.wireOp",EDGE,"E228"),sQuery(id+"F1.wireOp",EDGE,"E229"),sQuery(id+"F1.wireOp",EDGE,"E230"),sQuery(id+"F1.wireOp",EDGE,"E231"),sQuery(id+"F1.wireOp",EDGE,"E239"),sQuery(id+"F1.wireOp",EDGE,"E240"),sQuery(id+"F1.wireOp",EDGE,"E241"),sQuery(id+"F1.wireOp",EDGE,"E242"),sQuery(id+"F1.wireOp",EDGE,"E243"),sQuery(id+"F1.wireOp",EDGE,"E244"),sQuery(id+"F1.wireOp",EDGE,"E245"),sQuery(id+"F1.wireOp",EDGE,"E246"),sQuery(id+"F1.wireOp",EDGE,"E249"),sQuery(id+"F1.wireOp",EDGE,"E250"),sQuery(id+"F1.wireOp",EDGE,"E256"),sQuery(id+"F1.wireOp",EDGE,"E257"),sQuery(id+"F1.wireOp",EDGE,"E258"),sQuery(id+"F1.wireOp",EDGE,"E259"),sQuery(id+"F1.wireOp",EDGE,"E260"),sQuery(id+"F1.wireOp",EDGE,"E261"),sQuery(id+"F1.wireOp",EDGE,"E264"),sQuery(id+"F1.wireOp",EDGE,"E282"),sQuery(id+"F1.wireOp",EDGE,"E283"),sQuery(id+"F1.wireOp",EDGE,"E284"),sQuery(id+"F1.wireOp",EDGE,"E285"),sQuery(id+"F1.wireOp",EDGE,"E286"),sQuery(id+"F1.wireOp",EDGE,"E288"),sQuery(id+"F1.wireOp",EDGE,"E289"),sQuery(id+"F1.wireOp",EDGE,"E290"),sQuery(id+"F1.wireOp",EDGE,"E291"),sQuery(id+"F1.wireOp",EDGE,"E292"),sQuery(id+"F1.wireOp",EDGE,"E293"),sQuery(id+"F1.wireOp",EDGE,"E314"),sQuery(id+"F1.wireOp",EDGE,"E315"),sQuery(id+"F1.wireOp",EDGE,"E316"),sQuery(id+"F1.wireOp",EDGE,"E317"),sQuery(id+"F1.wireOp",EDGE,"E318"),sQuery(id+"F1.wireOp",EDGE,"E319"),sQuery(id+"F1.wireOp",EDGE,"E320"),sQuery(id+"F1.wireOp",EDGE,"E321"),sQuery(id+"F1.wireOp",EDGE,"E322"),sQuery(id+"F1.wireOp",EDGE,"E323"),sQuery(id+"F1.wireOp",EDGE,"E324"),sQuery(id+"F1.wireOp",EDGE,"E325"),sQuery(id+"F1.wireOp",EDGE,"E326"),sQuery(id+"F1.wireOp",EDGE,"E327"),sQuery(id+"F1.wireOp",EDGE,"E332"),sQuery(id+"F1.wireOp",EDGE,"E333"),sQuery(id+"F1.wireOp",EDGE,"E334"),sQuery(id+"F1.wireOp",EDGE,"E336"),sQuery(id+"F1.wireOp",EDGE,"E337"),sQuery(id+"F1.wireOp",EDGE,"E340"),sQuery(id+"F1.wireOp",EDGE,"E341"),sQuery(id+"F1.wireOp",EDGE,"E343"),sQuery(id+"F1.wireOp",EDGE,"E344"),sQuery(id+"F1.wireOp",EDGE,"E345"),sQuery(id+"F1.wireOp",EDGE,"E346"),sQuery(id+"F1.wireOp",EDGE,"E347"),sQuery(id+"F1.wireOp",EDGE,"E348"),sQuery(id+"F1.wireOp",EDGE,"E349"),sQuery(id+"F1.wireOp",EDGE,"E350"),sQuery(id+"F1.wireOp",EDGE,"E351"),sQuery(id+"F1.wireOp",EDGE,"E338"),sQuery(id+"F1.wireOp",EDGE,"E352"),sQuery(id+"F1.wireOp",EDGE,"E354"),sQuery(id+"F1.wireOp",EDGE,"E342"),sQuery(id+"F1.wireOp",EDGE,"E287"),sQuery(id+"F1.wireOp",EDGE,"E294"),sQuery(id+"F1.wireOp",EDGE,"E355"),sQuery(id+"F1.wireOp",EDGE,"E356"),sQuery(id+"F1.wireOp",EDGE,"E360"),sQuery(id+"F1.wireOp",EDGE,"E362"),sQuery(id+"F1.wireOp",EDGE,"E363"),sQuery(id+"F1.wireOp",EDGE,"E456"),sQuery(id+"F1.wireOp",EDGE,"E457"),sQuery(id+"F1.wireOp",EDGE,"E458"),sQuery(id+"F1.wireOp",EDGE,"E459"),sQuery(id+"F1.wireOp",EDGE,"E460"),sQuery(id+"F1.wireOp",EDGE,"E461"),sQuery(id+"F1.wireOp",EDGE,"E462"),sQuery(id+"F1.wireOp",EDGE,"E463"),sQuery(id+"F1.wireOp",EDGE,"E464"),sQuery(id+"F1.wireOp",EDGE,"E465"),sQuery(id+"F1.wireOp",EDGE,"E466"),sQuery(id+"F1.wireOp",EDGE,"E467"),sQuery(id+"F1.wireOp",EDGE,"E468"),sQuery(id+"F1.wireOp",EDGE,"E469"),sQuery(id+"F1.wireOp",EDGE,"E470"),sQuery(id+"F1.wireOp",EDGE,"E471"),sQuery(id+"F1.wireOp",EDGE,"E472"),sQuery(id+"F1.wireOp",EDGE,"E473"),sQuery(id+"F1.wireOp",EDGE,"E474"),sQuery(id+"F1.wireOp",EDGE,"E476"),sQuery(id+"F1.wireOp",EDGE,"E477"),sQuery(id+"F1.wireOp",EDGE,"E478"),sQuery(id+"F1.wireOp",EDGE,"E479"),sQuery(id+"F1.wireOp",EDGE,"E480"),sQuery(id+"F1.wireOp",EDGE,"E481"),sQuery(id+"F1.wireOp",EDGE,"E482"),sQuery(id+"F1.wireOp",EDGE,"E483"),sQuery(id+"F1.wireOp",EDGE,"E484"),sQuery(id+"F1.wireOp",EDGE,"E485"),sQuery(id+"F1.wireOp",EDGE,"E486"),sQuery(id+"F1.wireOp",EDGE,"E487"),sQuery(id+"F1.wireOp",EDGE,"E488"),sQuery(id+"F1.wireOp",EDGE,"E489"),sQuery(id+"F1.wireOp",EDGE,"E490"),sQuery(id+"F1.wireOp",EDGE,"E491"),sQuery(id+"F1.wireOp",EDGE,"E492"),sQuery(id+"F1.wireOp",EDGE,"E493"),sQuery(id+"F1.wireOp",EDGE,"E494"),sQuery(id+"F1.wireOp",EDGE,"E495"),sQuery(id+"F1.wireOp",EDGE,"E496"),sQuery(id+"F1.wireOp",EDGE,"E497"),sQuery(id+"F1.wireOp",EDGE,"E498"),sQuery(id+"F1.wireOp",EDGE,"E499"),sQuery(id+"F1.wireOp",EDGE,"E500"),sQuery(id+"F1.wireOp",EDGE,"E501"),sQuery(id+"F1.wireOp",EDGE,"E502"),sQuery(id+"F1.wireOp",EDGE,"E503"),sQuery(id+"F1.wireOp",EDGE,"E504"),sQuery(id+"F1.wireOp",EDGE,"E505"),sQuery(id+"F1.wireOp",EDGE,"E506"),sQuery(id+"F1.wireOp",EDGE,"E507"),sQuery(id+"F1.wireOp",EDGE,"E508"),sQuery(id+"F1.wireOp",EDGE,"E509"),sQuery(id+"F1.wireOp",EDGE,"E510"),sQuery(id+"F1.wireOp",EDGE,"E511"),sQuery(id+"F1.wireOp",EDGE,"E512"),sQuery(id+"F1.wireOp",EDGE,"E513"),sQuery(id+"F1.wireOp",EDGE,"E514"),sQuery(id+"F1.wireOp",EDGE,"E516"),sQuery(id+"F1.wireOp",EDGE,"E517"),sQuery(id+"F1.wireOp",EDGE,"E518"),sQuery(id+"F1.wireOp",EDGE,"E519"),sQuery(id+"F1.wireOp",EDGE,"E520"),sQuery(id+"F1.wireOp",EDGE,"E521"),sQuery(id+"F1.wireOp",EDGE,"E522"),sQuery(id+"F1.wireOp",EDGE,"E523"),sQuery(id+"F1.wireOp",EDGE,"E524"),sQuery(id+"F1.wireOp",EDGE,"E525"),sQuery(id+"F1.wireOp",EDGE,"E582"),sQuery(id+"F1.wireOp",EDGE,"E583"),sQuery(id+"F1.wireOp",EDGE,"E584"),sQuery(id+"F1.wireOp",EDGE,"E585"),sQuery(id+"F1.wireOp",EDGE,"E586"),sQuery(id+"F1.wireOp",EDGE,"E587"),sQuery(id+"F1.wireOp",EDGE,"E588"),sQuery(id+"F1.wireOp",EDGE,"E589"),sQuery(id+"F1.wireOp",EDGE,"E590"),sQuery(id+"F1.wireOp",EDGE,"E591"),sQuery(id+"F1.wireOp",EDGE,"E592"),sQuery(id+"F1.wireOp",EDGE,"E593"),sQuery(id+"F1.wireOp",EDGE,"E594"),sQuery(id+"F1.wireOp",EDGE,"E595"),sQuery(id+"F1.wireOp",EDGE,"E596"),sQuery(id+"F1.wireOp",EDGE,"E597"),sQuery(id+"F1.wireOp",EDGE,"E598"),sQuery(id+"F1.wireOp",EDGE,"E599"),sQuery(id+"F1.wireOp",EDGE,"E600"),sQuery(id+"F1.wireOp",EDGE,"E601"),sQuery(id+"F1.wireOp",EDGE,"E602"),sQuery(id+"F1.wireOp",EDGE,"E603"),sQuery(id+"F1.wireOp",EDGE,"E604"),sQuery(id+"F1.wireOp",EDGE,"E605"),sQuery(id+"F1.wireOp",EDGE,"E606"),sQuery(id+"F1.wireOp",EDGE,"E607"),sQuery(id+"F1.wireOp",EDGE,"E608"),sQuery(id+"F1.wireOp",EDGE,"E609"),sQuery(id+"F1.wireOp",EDGE,"E610"),sQuery(id+"F1.wireOp",EDGE,"E611"),sQuery(id+"F1.wireOp",EDGE,"E612"),sQuery(id+"F1.wireOp",EDGE,"E613"),sQuery(id+"F1.wireOp",EDGE,"E614"),sQuery(id+"F1.wireOp",EDGE,"E615"),sQuery(id+"F1.wireOp",EDGE,"E616"),sQuery(id+"F1.wireOp",EDGE,"E617"),sQuery(id+"F1.wireOp",EDGE,"E618"),sQuery(id+"F1.wireOp",EDGE,"E619"),sQuery(id+"F1.wireOp",EDGE,"E620"),sQuery(id+"F1.wireOp",EDGE,"E621"),sQuery(id+"F1.wireOp",EDGE,"E622"),sQuery(id+"F1.wireOp",EDGE,"E623"),sQuery(id+"F1.wireOp",EDGE,"E624"),sQuery(id+"F1.wireOp",EDGE,"E625"),sQuery(id+"F1.wireOp",EDGE,"E626"),sQuery(id+"F1.wireOp",EDGE,"E627"),sQuery(id+"F1.wireOp",EDGE,"E628"),sQuery(id+"F1.wireOp",EDGE,"E629"),sQuery(id+"F1.wireOp",EDGE,"E630"),sQuery(id+"F1.wireOp",EDGE,"E631"),sQuery(id+"F1.wireOp",EDGE,"E632"),sQuery(id+"F1.wireOp",EDGE,"E633"),sQuery(id+"F1.wireOp",EDGE,"E634"),sQuery(id+"F1.wireOp",EDGE,"E635"),sQuery(id+"F1.wireOp",EDGE,"E636"),sQuery(id+"F1.wireOp",EDGE,"E637"),sQuery(id+"F1.wireOp",EDGE,"E638"),sQuery(id+"F1.wireOp",EDGE,"E639"),sQuery(id+"F1.wireOp",EDGE,"E640"),sQuery(id+"F1.wireOp",EDGE,"E641"),sQuery(id+"F1.wireOp",EDGE,"E642"),sQuery(id+"F1.wireOp",EDGE,"E643"),sQuery(id+"F1.wireOp",EDGE,"E644"),sQuery(id+"F1.wireOp",EDGE,"E645"),sQuery(id+"F1.wireOp",EDGE,"E646"),sQuery(id+"F1.wireOp",EDGE,"E647"),sQuery(id+"F1.wireOp",EDGE,"E649"),sQuery(id+"F1.wireOp",EDGE,"E650")])],"isStart":false});
            extrude(context, id + "F3", {"entities" : qUnion([Q0, Q1, Q2, Q3, Q4, Q5, Q6, Q7, Q8, Q9, Q10, Q11, Q12, Q13, Q14, Q15, Q16, Q17, Q18, Q19, Q20, Q21, Q22, Q23, Q24]), "operationType" : NewBodyOperationType.ADD, "depth" : 4 * mm, "offsetDistance" : 25 * mm});
        }
        {
            var Q0;
            {var subQ0=sQuery(id+"F0.wireOp",EDGE,"E10");var subQ1=sQuery(id+"F0.wireOp",EDGE,"QIJiGY5w-lFCi-xx9X-rp0q-5GBFziIUs7mU");var subQ2=makeQuery(id+"F0.imprint","INTERSECT",VERTEX,{"derivedFrom":[subQ1,subQ0]});Q0=makeQuery(id+"F0.imprint","IMPRINT",FACE,{"disambiguationData":[TD([[makeQuery(id+"F0.imprint","IMPRINT",EDGE,{"disambiguationData":[TD([[subQ2,-1.0]])],"derivedFrom":subQ1}),1.0]])]});}
            var Q1;
            {var subQ0=sQuery(id+"F0.wireOp",EDGE,"E10");var subQ1=sQuery(id+"F0.wireOp",EDGE,"QIJiGY5w-lFCi-xx9X-rp0q-5GBFziIUs7mU");var subQ2=makeQuery(id+"F0.imprint","INTERSECT",VERTEX,{"derivedFrom":[subQ1,subQ0]});Q1=makeQuery(id+"F0.imprint","IMPRINT",FACE,{"disambiguationData":[TD([[makeQuery(id+"F0.imprint","IMPRINT",EDGE,{"disambiguationData":[TD([[subQ2,-1.0]])],"derivedFrom":subQ1}),-1.0]])]});}
            var Q2;
            {var subQ0=sQuery(id+"F0.wireOp",EDGE,"E10");var subQ1=sQuery(id+"F0.wireOp",EDGE,"E5");var subQ2=makeQuery(id+"F0.imprint","INTERSECT",VERTEX,{"disambiguationData":[OD(1.0)],"derivedFrom":[subQ1,subQ0]});Q2=makeQuery(id+"F0.imprint","IMPRINT",FACE,{"disambiguationData":[TD([[makeQuery(id+"F0.imprint","IMPRINT",EDGE,{"disambiguationData":[TD([[subQ2,1.0]])],"derivedFrom":subQ1}),1.0]])]});}
            var Q3;
            {var subQ0=sQuery(id+"F0.wireOp",EDGE,"E10");var subQ4=sQuery(id+"F0.wireOp",EDGE,"E5");var subQ5=makeQuery(id+"F0.imprint","INTERSECT",VERTEX,{"disambiguationData":[OD(0.0)],"derivedFrom":[subQ4,subQ0]});Q3=makeQuery(id+"F0.imprint","IMPRINT",FACE,{"disambiguationData":[TD([[makeQuery(id+"F0.imprint","IMPRINT",EDGE,{"disambiguationData":[TD([[subQ5,-1.0]])],"derivedFrom":subQ4}),1.0]])]});}
            var Q4;
            {var subQ0=sQuery(id+"F0.wireOp",EDGE,"E17");var subQ3=sQuery(id+"F0.wireOp",EDGE,"E5");var subQ7=makeQuery(id+"F0.imprint","INTERSECT",VERTEX,{"disambiguationData":[OD(0.0)],"derivedFrom":[subQ3,subQ0]});Q4=makeQuery(id+"F0.imprint","IMPRINT",FACE,{"disambiguationData":[TD([[makeQuery(id+"F0.imprint","IMPRINT",EDGE,{"disambiguationData":[TD([[subQ7,-1.0]])],"derivedFrom":subQ3}),1.0]])]});}
            var Q5;
            {var subQ0=sQuery(id+"F0.wireOp",EDGE,"E17");var subQ1=sQuery(id+"F0.wireOp",EDGE,"E5");var subQ2=makeQuery(id+"F0.imprint","INTERSECT",VERTEX,{"disambiguationData":[OD(0.0)],"derivedFrom":[subQ1,subQ0]});Q5=makeQuery(id+"F0.imprint","IMPRINT",FACE,{"disambiguationData":[TD([[makeQuery(id+"F0.imprint","IMPRINT",EDGE,{"disambiguationData":[TD([[subQ2,-1.0]])],"derivedFrom":subQ1}),-1.0]])]});}
            var Q6;
            {var subQ0=sQuery(id+"F0.wireOp",EDGE,"E11");var subQ1=sQuery(id+"F0.wireOp",EDGE,"b7w3sZkz-h2S3-PTXa-qy05-PL4N3AHQH3GV");var subQ2=makeQuery(id+"F0.imprint","INTERSECT",VERTEX,{"derivedFrom":[subQ1,subQ0]});Q6=makeQuery(id+"F0.imprint","IMPRINT",FACE,{"disambiguationData":[TD([[makeQuery(id+"F0.imprint","IMPRINT",EDGE,{"disambiguationData":[TD([[subQ2,-1.0]])],"derivedFrom":subQ1}),-1.0]])]});}
            var Q7;
            {var subQ0=sQuery(id+"F0.wireOp",EDGE,"E11");var subQ1=sQuery(id+"F0.wireOp",EDGE,"b7w3sZkz-h2S3-PTXa-qy05-PL4N3AHQH3GV");var subQ2=makeQuery(id+"F0.imprint","INTERSECT",VERTEX,{"derivedFrom":[subQ1,subQ0]});Q7=makeQuery(id+"F0.imprint","IMPRINT",FACE,{"disambiguationData":[TD([[makeQuery(id+"F0.imprint","IMPRINT",EDGE,{"disambiguationData":[TD([[subQ2,-1.0]])],"derivedFrom":subQ1}),1.0]])]});}
            var Q8;
            {var subQ0=sQuery(id+"F0.wireOp",EDGE,"E11");var subQ1=sQuery(id+"F0.wireOp",EDGE,"E5");var subQ2=makeQuery(id+"F0.imprint","INTERSECT",VERTEX,{"disambiguationData":[OD(0.0)],"derivedFrom":[subQ1,subQ0]});Q8=makeQuery(id+"F0.imprint","IMPRINT",FACE,{"disambiguationData":[TD([[makeQuery(id+"F0.imprint","IMPRINT",EDGE,{"disambiguationData":[TD([[subQ2,-1.0]])],"derivedFrom":subQ1}),1.0]])]});}
            var Q9;
            {var subQ0=sQuery(id+"F0.wireOp",EDGE,"E11");var subQ1=sQuery(id+"F0.wireOp",EDGE,"E5");var subQ2=makeQuery(id+"F0.imprint","INTERSECT",VERTEX,{"disambiguationData":[OD(1.0)],"derivedFrom":[subQ1,subQ0]});Q9=makeQuery(id+"F0.imprint","IMPRINT",FACE,{"disambiguationData":[TD([[makeQuery(id+"F0.imprint","IMPRINT",EDGE,{"disambiguationData":[TD([[subQ2,1.0]])],"derivedFrom":subQ1}),1.0]])]});}
            var Q10;
            {var subQ3=sQuery(id+"F0.wireOp",EDGE,"QIJiGY5w-lFCi-xx9X-rp0q-5GBFziIUs7mU");var subQ5=sQuery(id+"F0.wireOp",EDGE,"E19");var subQ6=makeQuery(id+"F0.imprint","INTERSECT",VERTEX,{"disambiguationData":[OD(1.0)],"derivedFrom":[subQ3,subQ5]});Q10=makeQuery(id+"F0.imprint","IMPRINT",FACE,{"disambiguationData":[TD([[makeQuery(id+"F0.imprint","IMPRINT",EDGE,{"disambiguationData":[TD([[subQ6,-1.0]])],"derivedFrom":subQ5}),-1.0]])]});}
            var Q11;
            {var subQ0=sQuery(id+"F0.wireOp",EDGE,"E19");var subQ6=sQuery(id+"F0.wireOp",EDGE,"QIJiGY5w-lFCi-xx9X-rp0q-5GBFziIUs7mU");var subQ8=makeQuery(id+"F0.imprint","INTERSECT",VERTEX,{"disambiguationData":[OD(0.0)],"derivedFrom":[subQ6,subQ0]});Q11=makeQuery(id+"F0.imprint","IMPRINT",FACE,{"disambiguationData":[TD([[makeQuery(id+"F0.imprint","IMPRINT",EDGE,{"disambiguationData":[TD([[subQ8,1.0]])],"derivedFrom":subQ0}),-1.0]])]});}
            var Q12;
            {var subQ0=sQuery(id+"F0.wireOp",EDGE,"QIJiGY5w-lFCi-xx9X-rp0q-5GBFziIUs7mU");var subQ5=sQuery(id+"F0.wireOp",EDGE,"E19");var subQ6=makeQuery(id+"F0.imprint","INTERSECT",VERTEX,{"disambiguationData":[OD(0.0)],"derivedFrom":[subQ0,subQ5]});Q12=makeQuery(id+"F0.imprint","IMPRINT",FACE,{"disambiguationData":[TD([[makeQuery(id+"F0.imprint","IMPRINT",EDGE,{"disambiguationData":[TD([[subQ6,-1.0]])],"derivedFrom":subQ5}),-1.0]])]});}
            var Q13;
            {var subQ0=sQuery(id+"F0.wireOp",EDGE,"E19");var subQ6=sQuery(id+"F0.wireOp",EDGE,"QIJiGY5w-lFCi-xx9X-rp0q-5GBFziIUs7mU");var subQ8=makeQuery(id+"F0.imprint","INTERSECT",VERTEX,{"disambiguationData":[OD(1.0)],"derivedFrom":[subQ6,subQ0]});Q13=makeQuery(id+"F0.imprint","IMPRINT",FACE,{"disambiguationData":[TD([[makeQuery(id+"F0.imprint","IMPRINT",EDGE,{"disambiguationData":[TD([[subQ8,1.0]])],"derivedFrom":subQ0}),-1.0]])]});}
            var Q14;
            {var subQ0=sQuery(id+"F0.wireOp",EDGE,"E16");var subQ4=sQuery(id+"F0.wireOp",EDGE,"E5");var subQ5=makeQuery(id+"F0.imprint","INTERSECT",VERTEX,{"disambiguationData":[OD(1.0)],"derivedFrom":[subQ4,subQ0]});Q14=makeQuery(id+"F0.imprint","IMPRINT",FACE,{"disambiguationData":[TD([[makeQuery(id+"F0.imprint","IMPRINT",EDGE,{"disambiguationData":[TD([[subQ5,1.0]])],"derivedFrom":subQ4}),1.0]])]});}
            var Q15;
            {var subQ0=sQuery(id+"F0.wireOp",EDGE,"E16");var subQ1=sQuery(id+"F0.wireOp",EDGE,"QIJiGY5w-lFCi-xx9X-rp0q-5GBFziIUs7mU");var subQ2=makeQuery(id+"F0.imprint","INTERSECT",VERTEX,{"derivedFrom":[subQ1,subQ0]});Q15=makeQuery(id+"F0.imprint","IMPRINT",FACE,{"disambiguationData":[TD([[makeQuery(id+"F0.imprint","IMPRINT",EDGE,{"disambiguationData":[TD([[subQ2,1.0]])],"derivedFrom":subQ1}),1.0]])]});}
            var Q16;
            {var subQ0=sQuery(id+"F0.wireOp",EDGE,"E16");var subQ1=sQuery(id+"F0.wireOp",EDGE,"QIJiGY5w-lFCi-xx9X-rp0q-5GBFziIUs7mU");var subQ2=makeQuery(id+"F0.imprint","INTERSECT",VERTEX,{"derivedFrom":[subQ1,subQ0]});Q16=makeQuery(id+"F0.imprint","IMPRINT",FACE,{"disambiguationData":[TD([[makeQuery(id+"F0.imprint","IMPRINT",EDGE,{"disambiguationData":[TD([[subQ2,1.0]])],"derivedFrom":subQ1}),-1.0]])]});}
            var Q17;
            {var subQ0=sQuery(id+"F0.wireOp",EDGE,"E16");var subQ4=sQuery(id+"F0.wireOp",EDGE,"E5");var subQ5=makeQuery(id+"F0.imprint","INTERSECT",VERTEX,{"disambiguationData":[OD(0.0)],"derivedFrom":[subQ4,subQ0]});Q17=makeQuery(id+"F0.imprint","IMPRINT",FACE,{"disambiguationData":[TD([[makeQuery(id+"F0.imprint","IMPRINT",EDGE,{"disambiguationData":[TD([[subQ5,-1.0]])],"derivedFrom":subQ4}),1.0]])]});}
            var Q18;
            {var subQ0=sQuery(id+"F0.wireOp",EDGE,"E15");var subQ1=sQuery(id+"F0.wireOp",EDGE,"E5");var subQ2=makeQuery(id+"F0.imprint","INTERSECT",VERTEX,{"disambiguationData":[OD(0.0)],"derivedFrom":[subQ1,subQ0]});Q18=makeQuery(id+"F0.imprint","IMPRINT",FACE,{"disambiguationData":[TD([[makeQuery(id+"F0.imprint","IMPRINT",EDGE,{"disambiguationData":[TD([[subQ2,-1.0]])],"derivedFrom":subQ1}),-1.0]])]});}
            var Q19;
            {var subQ0=sQuery(id+"F0.wireOp",EDGE,"E15");var subQ4=sQuery(id+"F0.wireOp",EDGE,"E5");var subQ8=makeQuery(id+"F0.imprint","INTERSECT",VERTEX,{"disambiguationData":[OD(0.0)],"derivedFrom":[subQ4,subQ0]});Q19=makeQuery(id+"F0.imprint","IMPRINT",FACE,{"disambiguationData":[TD([[makeQuery(id+"F0.imprint","IMPRINT",EDGE,{"disambiguationData":[TD([[subQ8,-1.0]])],"derivedFrom":subQ4}),1.0]])]});}
            var Q20;
            {var subQ0=sQuery(id+"F0.wireOp",EDGE,"E14");var subQ4=sQuery(id+"F0.wireOp",EDGE,"E5");var subQ5=makeQuery(id+"F0.imprint","INTERSECT",VERTEX,{"disambiguationData":[OD(1.0)],"derivedFrom":[subQ4,subQ0]});Q20=makeQuery(id+"F0.imprint","IMPRINT",FACE,{"disambiguationData":[TD([[makeQuery(id+"F0.imprint","IMPRINT",EDGE,{"disambiguationData":[TD([[subQ5,1.0]])],"derivedFrom":subQ4}),1.0]])]});}
            var Q21;
            {var subQ0=sQuery(id+"F0.wireOp",EDGE,"E14");var subQ1=sQuery(id+"F0.wireOp",EDGE,"b7w3sZkz-h2S3-PTXa-qy05-PL4N3AHQH3GV");var subQ2=makeQuery(id+"F0.imprint","INTERSECT",VERTEX,{"derivedFrom":[subQ1,subQ0]});Q21=makeQuery(id+"F0.imprint","IMPRINT",FACE,{"disambiguationData":[TD([[makeQuery(id+"F0.imprint","IMPRINT",EDGE,{"disambiguationData":[TD([[subQ2,1.0]])],"derivedFrom":subQ1}),1.0]])]});}
            var Q22;
            {var subQ0=sQuery(id+"F0.wireOp",EDGE,"E14");var subQ1=sQuery(id+"F0.wireOp",EDGE,"b7w3sZkz-h2S3-PTXa-qy05-PL4N3AHQH3GV");var subQ2=makeQuery(id+"F0.imprint","INTERSECT",VERTEX,{"derivedFrom":[subQ1,subQ0]});Q22=makeQuery(id+"F0.imprint","IMPRINT",FACE,{"disambiguationData":[TD([[makeQuery(id+"F0.imprint","IMPRINT",EDGE,{"disambiguationData":[TD([[subQ2,1.0]])],"derivedFrom":subQ1}),-1.0]])]});}
            var Q23;
            {var subQ0=sQuery(id+"F0.wireOp",EDGE,"E14");var subQ6=sQuery(id+"F0.wireOp",EDGE,"E5");var subQ7=makeQuery(id+"F0.imprint","INTERSECT",VERTEX,{"disambiguationData":[OD(0.0)],"derivedFrom":[subQ6,subQ0]});Q23=makeQuery(id+"F0.imprint","IMPRINT",FACE,{"disambiguationData":[TD([[makeQuery(id+"F0.imprint","IMPRINT",EDGE,{"disambiguationData":[TD([[subQ7,-1.0]])],"derivedFrom":subQ6}),1.0]])]});}
            extrude(context, id + "F4", {"entities" : qUnion([Q0, Q1, Q2, Q3, Q4, Q5, Q6, Q7, Q8, Q9, Q10, Q11, Q12, Q13, Q14, Q15, Q16, Q17, Q18, Q19, Q20, Q21, Q22, Q23]), "operationType" : NewBodyOperationType.ADD, "depth" : 3 * mm, "offsetDistance" : 25 * mm});
        }
        {
            var Q0;
            {var subQ0=sQuery(id+"F1.wireOp",EDGE,"E52");Q0=makeQuery(id+"F1.imprint","IMPRINT",FACE,{"disambiguationData":[TD([[makeQuery(id+"F1.imprint","IMPRINT",EDGE,{"derivedFrom":subQ0}),1.0]])]});}
            var Q1;
            {var subQ0=sQuery(id+"F1.wireOp",EDGE,"E108");Q1=makeQuery(id+"F1.imprint","IMPRINT",FACE,{"disambiguationData":[TD([[makeQuery(id+"F1.imprint","IMPRINT",EDGE,{"derivedFrom":subQ0}),1.0]])]});}
            var Q2;
            {var subQ0=sQuery(id+"F1.wireOp",EDGE,"E90");Q2=makeQuery(id+"F1.imprint","IMPRINT",FACE,{"disambiguationData":[TD([[makeQuery(id+"F1.imprint","IMPRINT",EDGE,{"derivedFrom":subQ0}),1.0]])]});}
            var Q3;
            {var subQ0=sQuery(id+"F1.wireOp",EDGE,"E58");Q3=makeQuery(id+"F1.imprint","IMPRINT",FACE,{"disambiguationData":[TD([[makeQuery(id+"F1.imprint","IMPRINT",EDGE,{"derivedFrom":subQ0}),-1.0]])]});}
            var Q4;
            {var subQ0=sQuery(id+"F1.wireOp",EDGE,"E62");var subQ1=sQuery(id+"F1.wireOp",EDGE,"E55");var subQ2=makeQuery(id+"F1.imprint","INTERSECT",VERTEX,{"derivedFrom":[subQ1,subQ0]});Q4=makeQuery(id+"F1.imprint","IMPRINT",FACE,{"disambiguationData":[TD([[makeQuery(id+"F1.imprint","IMPRINT",EDGE,{"disambiguationData":[TD([[subQ2,1.0]])],"derivedFrom":subQ1}),1.0]])]});}
            var Q5;
            {var subQ0=sQuery(id+"F1.wireOp",EDGE,"E57");Q5=makeQuery(id+"F1.imprint","IMPRINT",FACE,{"disambiguationData":[TD([[makeQuery(id+"F1.imprint","IMPRINT",EDGE,{"derivedFrom":subQ0}),1.0]])]});}
            var Q6;
            {var subQ0=sQuery(id+"F1.wireOp",EDGE,"E61");var subQ1=sQuery(id+"F1.wireOp",EDGE,"E55");var subQ2=makeQuery(id+"F1.imprint","INTERSECT",VERTEX,{"derivedFrom":[subQ1,subQ0]});Q6=makeQuery(id+"F1.imprint","IMPRINT",FACE,{"disambiguationData":[TD([[makeQuery(id+"F1.imprint","IMPRINT",EDGE,{"disambiguationData":[TD([[subQ2,-1.0]])],"derivedFrom":subQ1}),1.0]])]});}
            var Q7;
            {var subQ4=sQuery(id+"F1.wireOp",EDGE,"E53");Q7=makeQuery(id+"F1.imprint","IMPRINT",FACE,{"disambiguationData":[TD([[makeQuery(id+"F1.imprint","IMPRINT",EDGE,{"derivedFrom":subQ4}),1.0]])]});}
            extrude(context, id + "F5", {"entities" : qUnion([Q0, Q1, Q2, Q3, Q4, Q5, Q6, Q7]), "operationType" : NewBodyOperationType.ADD, "depth" : 8 * mm, "offsetDistance" : 25 * mm});
        }
        {
            var Q0;
            {var subQ3=sQuery(id+"F1.wireOp",EDGE,"ej4slr3Q-Yw2a-d8uW-XIuV-5FMGxbp2aJ1O");var subQ5=sQuery(id+"F1.wireOp",EDGE,"E74");var subQ7=makeQuery(id+"F1.imprint","INTERSECT",VERTEX,{"derivedFrom":[subQ5,subQ3]});Q0=makeQuery(id+"F1.imprint","IMPRINT",FACE,{"disambiguationData":[TD([[makeQuery(id+"F1.imprint","IMPRINT",EDGE,{"disambiguationData":[TD([[subQ7,-1.0]])],"derivedFrom":subQ5}),-1.0]])]});}
            extrude(context, id + "F6", {"entities" : qUnion([Q0]), "depth" : 8 * mm, "offsetDistance" : 25 * mm});
        }
        {
            var Q0;
            {var subQ0=sQuery(id+"F1.wireOp",EDGE,"E53");Q0=makeQuery(id+"F1.imprint","IMPRINT",FACE,{"disambiguationData":[TD([[makeQuery(id+"F1.imprint","IMPRINT",EDGE,{"derivedFrom":subQ0}),1.0]])]});}
            var sketch = newSketch(context, id + "F7", { "sketchPlane" : qUnion([Q0])});
            skPoint(sketch, "E651.0", {"position": v(-57.5, -67.99) * mm});
            skPoint(sketch, "E651.1", {"position": v(57.5, -67.99) * mm});
            skLineSegment(sketch, "E652.top", {"start": v(57.5, -123.98) * mm, "end": v(-57.5, -123.98) * mm});
            skLineSegment(sketch, "E652.left", {"start": v(57.5, -67.99) * mm, "end": v(57.5, -123.98) * mm});
            skLineSegment(sketch, "E652.right", {"start": v(-57.5, -67.98) * mm, "end": v(-57.5, -123.98) * mm});
            skPoint(sketch, "E653", {"position": v(-52.48, -71.6) * mm});
            skPoint(sketch, "E654", {"position": v(-52.45, -118.6) * mm});
            skPoint(sketch, "E655", {"position": v(-52.48, -106.35) * mm});
            skPoint(sketch, "E656", {"position": v(-52.54, -108.35) * mm});
            skPoint(sketch, "E657", {"position": v(-52.5, -81.85) * mm});
            skPoint(sketch, "E658", {"position": v(-52.5, -83.85) * mm});
            skPoint(sketch, "E659", {"position": v(-52.45, -94.1) * mm});
            skPoint(sketch, "E660", {"position": v(-52.48, -96.1) * mm});
            skPoint(sketch, "E661", {"position": v(-43.25, -67.98) * mm});
            skPoint(sketch, "E662", {"position": v(-34, -67.98) * mm});
            skPoint(sketch, "E663", {"position": v(-29.36, -67.98) * mm});
            skPoint(sketch, "E664", {"position": v(-24.73, -67.98) * mm});
            skPoint(sketch, "E665", {"position": v(-38.63, -67.98) * mm});
            skPoint(sketch, "E666", {"position": v(24.63, -67.98) * mm});
            skPoint(sketch, "E667", {"position": v(29.26, -67.98) * mm});
            skPoint(sketch, "E668", {"position": v(33.89, -67.98) * mm});
            skPoint(sketch, "E669", {"position": v(38.52, -67.98) * mm});
            skPoint(sketch, "E670", {"position": v(43.15, -67.99) * mm});
            skPoint(sketch, "E671", {"position": v(-8, -67.98) * mm});
            skPoint(sketch, "E672", {"position": v(-5.35, -67.98) * mm});
            skPoint(sketch, "E673", {"position": v(-2.72, -67.98) * mm});
            skPoint(sketch, "E674", {"position": v(0.01, -67.98) * mm});
            skPoint(sketch, "E675", {"position": v(2.57, -67.98) * mm});
            skPoint(sketch, "E676", {"position": v(5.25, -67.98) * mm});
            skPoint(sketch, "E677", {"position": v(7.82, -67.98) * mm});
            skArc(sketch, "E678", {"start": v(-8, -67.98) * mm, "mid": v(0.01, -75.99) * mm, "end": v(8.02, -67.98) * mm});
            skArc(sketch, "E679", {"start": v(-5.35, -67.98) * mm, "mid": v(-0.76, -73.29) * mm, "end": v(5.16, -69.5) * mm});
            skArc(sketch, "E680", {"start": v(-2.72, -67.98) * mm, "mid": v(-0.54, -70.66) * mm, "end": v(2.53, -69.05) * mm});
            skArc(sketch, "E681", {"start": v(-10.45, -67.98) * mm, "mid": v(0.01, -78.44) * mm, "end": v(10.47, -67.98) * mm});
            skArc(sketch, "E682", {"start": v(-8, -67.98) * mm, "mid": v(0.95, -60.02) * mm, "end": v(7.8, -69.85) * mm});
            skArc(sketch, "E683", {"start": v(-5.35, -67.98) * mm, "mid": v(0.78, -62.66) * mm, "end": v(5.16, -69.5) * mm});
            skArc(sketch, "E684", {"start": v(-2.72, -67.98) * mm, "mid": v(0.56, -65.3) * mm, "end": v(2.53, -69.05) * mm});
            skPoint(sketch, "E685", {"position": v(-36.31, -67.98) * mm});
            skArc(sketch, "E686", {"start": v(-36.31, -67.98) * mm, "mid": v(-34, -65.66) * mm, "end": v(-31.69, -67.98) * mm});
            skArc(sketch, "E687", {"start": v(-38.63, -67.98) * mm, "mid": v(-34, -63.35) * mm, "end": v(-29.37, -67.98) * mm});
            skLineSegment(sketch, "E688", {"start": v(-34, -67.98) * mm, "end": v(-34, -67.98) * mm});
            skArc(sketch, "E689", {"start": v(15.3, -67.98) * mm, "mid": v(33.89, -49.4) * mm, "end": v(52.46, -67.98) * mm});
            skArc(sketch, "E690", {"start": v(24.63, -67.98) * mm, "mid": v(33.89, -58.72) * mm, "end": v(43.15, -67.98) * mm});
            skArc(sketch, "E691", {"start": v(29.26, -67.98) * mm, "mid": v(33.89, -63.35) * mm, "end": v(38.52, -67.98) * mm});
            skArc(sketch, "E692", {"start": v(31.57, -67.98) * mm, "mid": v(33.89, -65.67) * mm, "end": v(36.2, -67.98) * mm});
            skPoint(sketch, "E693", {"position": v(-47.87, -71.6) * mm});
            skPoint(sketch, "E694", {"position": v(-47.87, -67.98) * mm});
            skPoint(sketch, "E695", {"position": v(-43.24, -71.6) * mm});
            skPoint(sketch, "E696", {"position": v(-38.66, -71.6) * mm});
            skPoint(sketch, "E697", {"position": v(-36.32, -71.6) * mm});
            skPoint(sketch, "E698", {"position": v(-33.97, -71.6) * mm});
            skPoint(sketch, "E699", {"position": v(-31.68, -71.6) * mm});
            skPoint(sketch, "E700", {"position": v(-29.37, -71.6) * mm});
            skPoint(sketch, "E701", {"position": v(-24.77, -71.6) * mm});
            skLineSegment(sketch, "E702.top", {"start": v(-43.26, -71.6) * mm, "end": v(-38.66, -71.6) * mm});
            skLineSegment(sketch, "E703.top", {"start": v(-29.37, -71.6) * mm, "end": v(-24.77, -71.6) * mm});
            skPoint(sketch, "E704", {"position": v(-43.23, -81.85) * mm});
            skPoint(sketch, "E705", {"position": v(-38.62, -81.85) * mm});
            skPoint(sketch, "E706", {"position": v(-36.3, -81.85) * mm});
            skPoint(sketch, "E707", {"position": v(-34, -81.85) * mm});
            skPoint(sketch, "E708", {"position": v(-31.67, -81.85) * mm});
            skPoint(sketch, "E709", {"position": v(-29.36, -81.85) * mm});
            skPoint(sketch, "E710", {"position": v(-43.18, -83.85) * mm});
            skPoint(sketch, "E711", {"position": v(-38.64, -83.85) * mm});
            skPoint(sketch, "E712", {"position": v(-36.32, -83.85) * mm});
            skPoint(sketch, "E713", {"position": v(-34, -83.85) * mm});
            skPoint(sketch, "E714", {"position": v(-31.68, -83.85) * mm});
            skPoint(sketch, "E715", {"position": v(-29.37, -83.85) * mm});
            skPoint(sketch, "E716", {"position": v(-47.9, -81.85) * mm});
            skPoint(sketch, "E717", {"position": v(-47.87, -83.85) * mm});
            skLineSegment(sketch, "E718", {"start": v(-52.5, -81.85) * mm, "end": v(-47.9, -81.85) * mm});
            skLineSegment(sketch, "E719", {"start": v(-47.87, -83.85) * mm, "end": v(-52.5, -83.85) * mm});
            skPoint(sketch, "E720", {"position": v(-47.91, -94.1) * mm});
            skPoint(sketch, "E721", {"position": v(-47.88, -96.1) * mm});
            skPoint(sketch, "E722", {"position": v(-43.2, -94.1) * mm});
            skPoint(sketch, "E723", {"position": v(-43.2, -96.1) * mm});
            skPoint(sketch, "E724", {"position": v(-38.61, -94.1) * mm});
            skPoint(sketch, "E725", {"position": v(-36.31, -94.1) * mm});
            skPoint(sketch, "E726", {"position": v(-34.02, -94.1) * mm});
            skPoint(sketch, "E727", {"position": v(-31.68, -94.1) * mm});
            skPoint(sketch, "E728", {"position": v(-29.38, -94.1) * mm});
            skPoint(sketch, "E729", {"position": v(-24.75, -94.1) * mm});
            skPoint(sketch, "E730", {"position": v(-38.61, -96.1) * mm});
            skPoint(sketch, "E731", {"position": v(-36.31, -96.1) * mm});
            skPoint(sketch, "E732", {"position": v(-34.02, -96.1) * mm});
            skPoint(sketch, "E733", {"position": v(-31.68, -96.1) * mm});
            skPoint(sketch, "E734", {"position": v(-29.38, -96.1) * mm});
            skPoint(sketch, "E735", {"position": v(-24.75, -96.1) * mm});
            skPoint(sketch, "E736", {"position": v(-47.98, -106.35) * mm});
            skPoint(sketch, "E737", {"position": v(-43.2, -106.35) * mm});
            skPoint(sketch, "E738", {"position": v(-38.66, -106.35) * mm});
            skPoint(sketch, "E739", {"position": v(-36.36, -106.35) * mm});
            skPoint(sketch, "E740", {"position": v(-34.06, -106.35) * mm});
            skPoint(sketch, "E741", {"position": v(-31.68, -106.35) * mm});
            skPoint(sketch, "E742", {"position": v(-29.4, -106.35) * mm});
            skPoint(sketch, "E743", {"position": v(-24.74, -106.35) * mm});
            skPoint(sketch, "E744", {"position": v(-47.98, -108.35) * mm});
            skPoint(sketch, "E745", {"position": v(-43.2, -108.35) * mm});
            skPoint(sketch, "E746", {"position": v(-38.72, -108.35) * mm});
            skPoint(sketch, "E747", {"position": v(-36.33, -108.35) * mm});
            skPoint(sketch, "E748", {"position": v(-34.06, -108.35) * mm});
            skPoint(sketch, "E749", {"position": v(-31.68, -108.35) * mm});
            skPoint(sketch, "E750", {"position": v(-29.4, -108.35) * mm});
            skPoint(sketch, "E751", {"position": v(-24.74, -108.35) * mm});
            skPoint(sketch, "E752", {"position": v(-47.92, -118.6) * mm});
            skPoint(sketch, "E753", {"position": v(-43.2, -118.6) * mm});
            skPoint(sketch, "E754", {"position": v(-38.72, -118.6) * mm});
            skPoint(sketch, "E755", {"position": v(-36.33, -118.6) * mm});
            skPoint(sketch, "E756", {"position": v(-34.06, -118.6) * mm});
            skPoint(sketch, "E757", {"position": v(-31.68, -118.6) * mm});
            skPoint(sketch, "E758", {"position": v(-29.4, -118.6) * mm});
            skPoint(sketch, "E759", {"position": v(-24.74, -118.6) * mm});
            skLineSegment(sketch, "E760", {"start": v(-52.54, -108.35) * mm, "end": v(-47.98, -108.35) * mm});
            skLineSegment(sketch, "E761", {"start": v(-47.92, -118.6) * mm, "end": v(-52.45, -118.6) * mm});
            skLineSegment(sketch, "E762", {"start": v(-43.2, -108.35) * mm, "end": v(-38.72, -108.35) * mm});
            skLineSegment(sketch, "E763", {"start": v(-38.72, -118.6) * mm, "end": v(-43.2, -118.6) * mm});
            skLineSegment(sketch, "E764", {"start": v(-47.87, -71.6) * mm, "end": v(-52.48, -71.6) * mm});
            skLineSegment(sketch, "E765.top", {"start": v(-52.5, -71.6) * mm, "end": v(-47.87, -71.6) * mm});
            skLineSegment(sketch, "E766.bottom", {"start": v(-52.5, -81.85) * mm, "end": v(-47.87, -81.85) * mm});
            skLineSegment(sketch, "E766.top", {"start": v(-52.5, -83.85) * mm, "end": v(-47.87, -83.85) * mm});
            skLineSegment(sketch, "E767.left", {"start": v(-38.66, -71.6) * mm, "end": v(-38.66, -81.85) * mm});
            skLineSegment(sketch, "E768.left", {"start": v(-38.64, -83.85) * mm, "end": v(-38.64, -94.1) * mm});
            skLineSegment(sketch, "E768.right", {"start": v(-36.31, -83.85) * mm, "end": v(-36.31, -94.1) * mm});
            skLineSegment(sketch, "E769.bottom", {"start": v(-52.45, -94.1) * mm, "end": v(-47.88, -94.1) * mm});
            skLineSegment(sketch, "E769.top", {"start": v(-52.5, -96.1) * mm, "end": v(-47.88, -96.1) * mm});
            skLineSegment(sketch, "E770.bottom", {"start": v(-52.48, -106.35) * mm, "end": v(-47.98, -106.35) * mm});
            skLineSegment(sketch, "E770.top", {"start": v(-52.48, -108.35) * mm, "end": v(-47.98, -108.35) * mm});
            skLineSegment(sketch, "E771.top", {"start": v(-52.45, -123.98) * mm, "end": v(-24.8, -123.98) * mm});
            skLineSegment(sketch, "E772.left", {"start": v(-38.61, -96.1) * mm, "end": v(-38.66, -106.35) * mm});
            skLineSegment(sketch, "E772.right", {"start": v(-36.31, -96.1) * mm, "end": v(-36.36, -106.35) * mm});
            skLineSegment(sketch, "E773", {"start": v(-38.72, -108.35) * mm, "end": v(-38.72, -118.6) * mm});
            skLineSegment(sketch, "E774", {"start": v(-36.33, -118.6) * mm, "end": v(-36.33, -108.35) * mm});
            skLineSegment(sketch, "E775", {"start": v(-29.37, -71.6) * mm, "end": v(-29.36, -81.85) * mm});
            skLineSegment(sketch, "E776", {"start": v(-29.37, -83.85) * mm, "end": v(-29.38, -94.1) * mm});
            skLineSegment(sketch, "E777", {"start": v(-29.38, -96.1) * mm, "end": v(-29.4, -106.35) * mm});
            skLineSegment(sketch, "E778", {"start": v(-29.4, -108.35) * mm, "end": v(-29.4, -118.6) * mm});
            skLineSegment(sketch, "E779", {"start": v(-43.18, -83.85) * mm, "end": v(-38.64, -83.85) * mm});
            skLineSegment(sketch, "E780", {"start": v(-43.23, -81.85) * mm, "end": v(-38.66, -81.85) * mm});
            skPoint(sketch, "E781", {"position": v(-24.74, -81.82) * mm});
            skLineSegment(sketch, "E782", {"start": v(-29.37, -83.85) * mm, "end": v(-24.74, -83.86) * mm});
            skLineSegment(sketch, "E783", {"start": v(-36.31, -83.85) * mm, "end": v(-31.68, -83.85) * mm});
            skLineSegment(sketch, "E784", {"start": v(-36.3, -81.85) * mm, "end": v(-31.67, -81.85) * mm});
            skLineSegment(sketch, "E785", {"start": v(-31.68, -83.85) * mm, "end": v(-31.68, -94.1) * mm});
            skLineSegment(sketch, "E786", {"start": v(-29.36, -81.85) * mm, "end": v(-24.74, -81.82) * mm});
            skLineSegment(sketch, "E787", {"start": v(-52.48, -71.6) * mm, "end": v(-52.5, -81.85) * mm});
            skLineSegment(sketch, "E788", {"start": v(-47.98, -108.35) * mm, "end": v(-47.92, -118.6) * mm});
            skLineSegment(sketch, "E789", {"start": v(-31.68, -108.35) * mm, "end": v(-31.68, -118.6) * mm});
            skLineSegment(sketch, "E790", {"start": v(-31.68, -96.1) * mm, "end": v(-31.68, -106.35) * mm});
            skLineSegment(sketch, "E791", {"start": v(-29.4, -118.6) * mm, "end": v(-24.8, -118.6) * mm});
            skLineSegment(sketch, "E792", {"start": v(-36.33, -118.6) * mm, "end": v(-31.68, -118.6) * mm});
            skPoint(sketch, "E793", {"position": v(-20.11, -94.1) * mm});
            skPoint(sketch, "E794", {"position": v(-15.49, -94.1) * mm});
            skPoint(sketch, "E795", {"position": v(-20.11, -96.1) * mm});
            skPoint(sketch, "E796", {"position": v(-15.49, -96.1) * mm});
            skLineSegment(sketch, "E797", {"start": v(-29.38, -94.1) * mm, "end": v(-24.75, -94.1) * mm});
            skLineSegment(sketch, "E798", {"start": v(-20.11, -94.1) * mm, "end": v(-15.49, -94.1) * mm});
            skLineSegment(sketch, "E799", {"start": v(-29.38, -96.1) * mm, "end": v(-24.75, -96.1) * mm});
            skLineSegment(sketch, "E800", {"start": v(-20.11, -96.1) * mm, "end": v(-15.49, -96.1) * mm});
            skLineSegment(sketch, "E801", {"start": v(-43.2, -94.1) * mm, "end": v(-38.64, -94.1) * mm});
            skLineSegment(sketch, "E802", {"start": v(-43.2, -96.1) * mm, "end": v(-38.61, -96.1) * mm});
            skLineSegment(sketch, "E803", {"start": v(-36.31, -94.1) * mm, "end": v(-31.68, -94.1) * mm});
            skLineSegment(sketch, "E804", {"start": v(-36.31, -96.1) * mm, "end": v(-31.68, -96.1) * mm});
            skPoint(sketch, "E805", {"position": v(-20.1, -106.35) * mm});
            skPoint(sketch, "E806", {"position": v(-20.1, -108.35) * mm});
            skPoint(sketch, "E807", {"position": v(-15.52, -106.35) * mm});
            skPoint(sketch, "E808", {"position": v(-15.52, -108.35) * mm});
            skLineSegment(sketch, "E809", {"start": v(-29.4, -106.35) * mm, "end": v(-24.74, -106.35) * mm});
            skLineSegment(sketch, "E810", {"start": v(-20.1, -106.35) * mm, "end": v(-15.52, -106.35) * mm});
            skLineSegment(sketch, "E811", {"start": v(-29.4, -108.35) * mm, "end": v(-24.74, -108.35) * mm});
            skLineSegment(sketch, "E812", {"start": v(-36.33, -108.35) * mm, "end": v(-31.68, -108.35) * mm});
            skLineSegment(sketch, "E813", {"start": v(-36.36, -106.35) * mm, "end": v(-31.68, -106.35) * mm});
            skLineSegment(sketch, "E814", {"start": v(-43.2, -106.35) * mm, "end": v(-38.66, -106.35) * mm});
            skLineSegment(sketch, "E815", {"start": v(-20.1, -108.35) * mm, "end": v(-15.52, -108.35) * mm});
            skLineSegment(sketch, "E816", {"start": v(-20.05, -118.53) * mm, "end": v(-15.5, -118.53) * mm});
            skPoint(sketch, "E817", {"position": v(-20.08, -81.8) * mm});
            skPoint(sketch, "E818", {"position": v(-20.08, -83.8) * mm});
            skPoint(sketch, "E819", {"position": v(-15.53, -81.8) * mm});
            skPoint(sketch, "E820", {"position": v(-15.53, -83.8) * mm});
            skLineSegment(sketch, "E821", {"start": v(-20.08, -81.8) * mm, "end": v(-15.53, -81.8) * mm});
            skLineSegment(sketch, "E822", {"start": v(-20.08, -83.8) * mm, "end": v(-15.53, -83.8) * mm});
            skLineSegment(sketch, "E823", {"start": v(-36.3, -71.6) * mm, "end": v(-31.68, -71.6) * mm});
            skLineSegment(sketch, "E824", {"start": v(-43.24, -71.6) * mm, "end": v(-38.66, -71.6) * mm});
            skLineSegment(sketch, "E825", {"start": v(-36.3, -71.6) * mm, "end": v(-36.3, -81.85) * mm});
            skLineSegment(sketch, "E826", {"start": v(-36.31, -67.98) * mm, "end": v(-36.31, -69.55) * mm});
            skLineSegment(sketch, "E827", {"start": v(-24.74, -118.6) * mm, "end": v(-15.5, -118.53) * mm});
            skLineSegment(sketch, "E828", {"start": v(-29.4, -118.6) * mm, "end": v(-24.74, -118.6) * mm});
            skLineSegment(sketch, "E829", {"start": v(-31.69, -67.98) * mm, "end": v(-31.68, -69.55) * mm});
            skLineSegment(sketch, "E830", {"start": v(-31.68, -71.6) * mm, "end": v(-31.67, -81.85) * mm});
            skPoint(sketch, "E831", {"position": v(-26.93, -50.9) * mm});
            skLineSegment(sketch, "E832", {"start": v(-50.57, -59.32) * mm, "end": v(-50.6, -59.3) * mm});
            skLineSegment(sketch, "E833", {"start": v(-34, -49.49) * mm, "end": v(-34, -67.98) * mm});
            skLineSegment(sketch, "E834", {"start": v(-41.1, -50.84) * mm, "end": v(-34, -67.98) * mm});
            skLineSegment(sketch, "E835", {"start": v(-26.93, -50.9) * mm, "end": v(-34, -67.98) * mm});
            skPoint(sketch, "E836", {"position": v(-51.12, -60.89) * mm});
            skLineSegment(sketch, "E837", {"start": v(-20.92, -54.9) * mm, "end": v(-34, -67.98) * mm});
            skPoint(sketch, "E838", {"position": v(-20.09, -67.93) * mm});
            skLineSegment(sketch, "E839", {"start": v(-47.06, -54.91) * mm, "end": v(-34, -67.98) * mm});
            skLineSegment(sketch, "E840", {"start": v(-52.5, -83.85) * mm, "end": v(-52.45, -94.1) * mm});
            skLineSegment(sketch, "E841", {"start": v(-47.87, -83.85) * mm, "end": v(-47.88, -94.1) * mm});
            skLineSegment(sketch, "E842", {"start": v(-43.18, -83.85) * mm, "end": v(-43.2, -94.1) * mm});
            skLineSegment(sketch, "E843", {"start": v(-52.5, -96.1) * mm, "end": v(-52.48, -106.35) * mm});
            skLineSegment(sketch, "E844", {"start": v(-47.88, -96.1) * mm, "end": v(-47.98, -106.35) * mm});
            skLineSegment(sketch, "E845", {"start": v(-43.2, -96.1) * mm, "end": v(-43.2, -106.35) * mm});
            skLineSegment(sketch, "E846", {"start": v(-52.48, -108.35) * mm, "end": v(-52.45, -118.6) * mm});
            skLineSegment(sketch, "E847", {"start": v(-43.2, -108.35) * mm, "end": v(-43.2, -118.6) * mm});
            skLineSegment(sketch, "E848", {"start": v(-24.74, -108.35) * mm, "end": v(-24.74, -118.6) * mm});
            skLineSegment(sketch, "E849", {"start": v(-24.75, -96.1) * mm, "end": v(-24.74, -106.35) * mm});
            skLineSegment(sketch, "E850", {"start": v(-20.1, -108.35) * mm, "end": v(-20.05, -118.53) * mm});
            skLineSegment(sketch, "E851", {"start": v(-15.52, -108.35) * mm, "end": v(-15.5, -118.53) * mm});
            skLineSegment(sketch, "E852", {"start": v(-20.11, -96.1) * mm, "end": v(-20.1, -106.35) * mm});
            skLineSegment(sketch, "E853", {"start": v(-15.49, -96.1) * mm, "end": v(-15.52, -106.35) * mm});
            skLineSegment(sketch, "E854", {"start": v(-24.74, -83.86) * mm, "end": v(-24.75, -94.1) * mm});
            skLineSegment(sketch, "E855", {"start": v(-20.08, -83.8) * mm, "end": v(-20.11, -94.1) * mm});
            skLineSegment(sketch, "E856", {"start": v(-15.53, -83.8) * mm, "end": v(-15.49, -94.1) * mm});
            skLineSegment(sketch, "E857", {"start": v(-24.77, -71.6) * mm, "end": v(-24.74, -81.82) * mm});
            skLineSegment(sketch, "E858", {"start": v(-43.24, -71.6) * mm, "end": v(-43.23, -81.85) * mm});
            skLineSegment(sketch, "E859", {"start": v(-47.87, -71.6) * mm, "end": v(-47.87, -81.85) * mm});
            skLineSegment(sketch, "E860", {"start": v(-52.52, -67.95) * mm, "end": v(-15.48, -67.95) * mm});
            skLineSegment(sketch, "E861", {"start": v(-36.31, -69.55) * mm, "end": v(-31.68, -69.55) * mm});
            skLineSegment(sketch, "E862", {"start": v(-34, -67.98) * mm, "end": v(-10.45, -67.98) * mm});
            skLineSegment(sketch, "E863", {"start": v(-51.12, -60.89) * mm, "end": v(-34, -67.98) * mm});
            skLineSegment(sketch, "E864", {"start": v(-34, -67.98) * mm, "end": v(-16.91, -60.9) * mm});
            skPoint(sketch, "E865", {"position": v(-16.91, -60.9) * mm});
            skLineSegment(sketch, "E866", {"start": v(33.89, -67.98) * mm, "end": v(51.05, -60.87) * mm});
            skPoint(sketch, "E867", {"position": v(51.05, -60.87) * mm});
            skLineSegment(sketch, "E868", {"start": v(33.89, -67.98) * mm, "end": v(47.02, -54.84) * mm});
            skLineSegment(sketch, "E869", {"start": v(33.89, -67.98) * mm, "end": v(41, -50.82) * mm});
            skLineSegment(sketch, "E870", {"start": v(33.89, -49.4) * mm, "end": v(33.89, -67.98) * mm});
            skLineSegment(sketch, "E871", {"start": v(26.78, -50.82) * mm, "end": v(33.89, -67.98) * mm});
            skLineSegment(sketch, "E872", {"start": v(20.75, -54.84) * mm, "end": v(33.89, -67.98) * mm});
            skLineSegment(sketch, "E873", {"start": v(16.72, -60.87) * mm, "end": v(33.89, -67.98) * mm});
            skPoint(sketch, "E874", {"position": v(20.04, -67.98) * mm});
            skPoint(sketch, "E875", {"position": v(24.72, -118.58) * mm});
            skPoint(sketch, "E876", {"position": v(29.35, -118.58) * mm});
            skPoint(sketch, "E877", {"position": v(43.15, -118.58) * mm});
            skLineSegment(sketch, "E878", {"start": v(-5.35, -67.98) * mm, "end": v(-5.35, -118.47) * mm});
            skLineSegment(sketch, "E879", {"start": v(5.16, -69.5) * mm, "end": v(5.16, -118.47) * mm});
            skLineSegment(sketch, "E880", {"start": v(-10.45, -67.98) * mm, "end": v(10.47, -67.98) * mm});
            skLineSegment(sketch, "E881", {"start": v(0.01, -67.98) * mm, "end": v(9.48, -64.05) * mm});
            skLineSegment(sketch, "E882", {"start": v(0.01, -67.98) * mm, "end": v(7.34, -60.65) * mm});
            skLineSegment(sketch, "E883", {"start": v(0.01, -67.98) * mm, "end": v(4.03, -58.29) * mm});
            skLineSegment(sketch, "E884", {"start": v(0.01, -67.98) * mm, "end": v(0.01, -57.48) * mm});
            skLineSegment(sketch, "E885", {"start": v(0.01, -67.98) * mm, "end": v(-4, -58.3) * mm});
            skLineSegment(sketch, "E886", {"start": v(0.01, -67.98) * mm, "end": v(-7.45, -60.5) * mm});
            skLineSegment(sketch, "E887", {"start": v(0.01, -67.98) * mm, "end": v(-9.77, -63.92) * mm});
            skPoint(sketch, "E888", {"position": v(-10.44, -83.84) * mm});
            skPoint(sketch, "E889", {"position": v(-8, -83.84) * mm});
            skPoint(sketch, "E890", {"position": v(-5.35, -83.84) * mm});
            skPoint(sketch, "E891", {"position": v(-2.72, -83.84) * mm});
            skPoint(sketch, "E892", {"position": v(2.53, -83.84) * mm});
            skPoint(sketch, "E893", {"position": v(5.16, -83.84) * mm});
            skPoint(sketch, "E894", {"position": v(7.8, -83.84) * mm});
            skPoint(sketch, "E895", {"position": v(10.48, -83.84) * mm});
            skPoint(sketch, "E896", {"position": v(15.56, -83.84) * mm});
            skPoint(sketch, "E897", {"position": v(20.13, -83.84) * mm});
            skPoint(sketch, "E898", {"position": v(24.75, -83.84) * mm});
            skPoint(sketch, "E899", {"position": v(29.34, -83.84) * mm});
            skPoint(sketch, "E900", {"position": v(31.57, -83.84) * mm});
            skPoint(sketch, "E901", {"position": v(33.85, -83.84) * mm});
            skPoint(sketch, "E902", {"position": v(36.2, -83.84) * mm});
            skPoint(sketch, "E903", {"position": v(38.52, -83.84) * mm});
            skPoint(sketch, "E904", {"position": v(43.15, -83.84) * mm});
            skPoint(sketch, "E905", {"position": v(47.76, -83.84) * mm});
            skLineSegment(sketch, "E906", {"start": v(15.56, -83.84) * mm, "end": v(15.56, -94.04) * mm});
            skLineSegment(sketch, "E907", {"start": v(15.56, -94.04) * mm, "end": v(20.13, -94.04) * mm});
            skLineSegment(sketch, "E908", {"start": v(20.13, -94.04) * mm, "end": v(20.13, -83.84) * mm});
            skLineSegment(sketch, "E909", {"start": v(24.75, -83.84) * mm, "end": v(24.75, -94.04) * mm});
            skLineSegment(sketch, "E910", {"start": v(24.75, -94.04) * mm, "end": v(29.35, -94.04) * mm});
            skLineSegment(sketch, "E911", {"start": v(29.35, -94.04) * mm, "end": v(29.34, -83.84) * mm});
            skLineSegment(sketch, "E912", {"start": v(15.56, -81.78) * mm, "end": v(20.13, -81.78) * mm});
            skLineSegment(sketch, "E913", {"start": v(24.75, -81.78) * mm, "end": v(29.34, -81.78) * mm});
            skLineSegment(sketch, "E914", {"start": v(31.67, -81.78) * mm, "end": v(34.05, -81.78) * mm});
            skLineSegment(sketch, "E915", {"start": v(34.05, -81.78) * mm, "end": v(36.3, -81.78) * mm});
            skLineSegment(sketch, "E916", {"start": v(43.15, -81.84) * mm, "end": v(43.15, -81.84) * mm});
            skPoint(sketch, "E917", {"position": v(28.54, -55.08) * mm});
            skPoint(sketch, "E918", {"position": v(33.89, -54.05) * mm});
            skPoint(sketch, "E919", {"position": v(39.2, -55.14) * mm});
            skPoint(sketch, "E920", {"position": v(43.75, -58.11) * mm});
            skPoint(sketch, "E921", {"position": v(47.02, -54.84) * mm});
            skPoint(sketch, "E922", {"position": v(24.07, -58.16) * mm});
            skPoint(sketch, "E923", {"position": v(27.34, -61.43) * mm});
            skPoint(sketch, "E924", {"position": v(30.33, -59.4) * mm});
            skPoint(sketch, "E925", {"position": v(33.89, -58.7) * mm});
            skPoint(sketch, "E926", {"position": v(37.43, -59.43) * mm});
            skPoint(sketch, "E927", {"position": v(40.43, -61.43) * mm});
            skPoint(sketch, "E928", {"position": v(42.47, -64.43) * mm});
            skPoint(sketch, "E929", {"position": v(46.73, -62.66) * mm});
            skPoint(sketch, "E930", {"position": v(25.33, -64.44) * mm});
            skPoint(sketch, "E931", {"position": v(21.05, -62.66) * mm});
            skPoint(sketch, "E932", {"position": v(16.72, -60.87) * mm});
            skPoint(sketch, "E933", {"position": v(15.3, -67.98) * mm});
            skPoint(sketch, "E934", {"position": v(15.56, -71.59) * mm});
            skPoint(sketch, "E935", {"position": v(20.13, -71.59) * mm});
            skPoint(sketch, "E936", {"position": v(24.74, -71.59) * mm});
            skPoint(sketch, "E937", {"position": v(29.33, -71.59) * mm});
            skPoint(sketch, "E938", {"position": v(31.67, -71.59) * mm});
            skPoint(sketch, "E939", {"position": v(33.95, -71.59) * mm});
            skPoint(sketch, "E940", {"position": v(36.3, -71.59) * mm});
            skPoint(sketch, "E941", {"position": v(43.15, -71.59) * mm});
            skLineSegment(sketch, "E942", {"start": v(31.67, -71.59) * mm, "end": v(36.3, -71.59) * mm});
            skLineSegment(sketch, "E943", {"start": v(24.74, -71.59) * mm, "end": v(24.75, -81.78) * mm});
            skLineSegment(sketch, "E944.bottom", {"start": v(15.53, -96.12) * mm, "end": v(20.13, -96.12) * mm});
            skLineSegment(sketch, "E944.top", {"start": v(15.53, -106.37) * mm, "end": v(20.13, -106.37) * mm});
            skLineSegment(sketch, "E944.left", {"start": v(15.53, -96.12) * mm, "end": v(15.53, -106.37) * mm});
            skLineSegment(sketch, "E944.right", {"start": v(20.13, -96.12) * mm, "end": v(20.13, -106.37) * mm});
            skPoint(sketch, "E945", {"position": v(24.7, -106.28) * mm});
            skPoint(sketch, "E946", {"position": v(29.3, -106.32) * mm});
            skPoint(sketch, "E947", {"position": v(31.67, -106.28) * mm});
            skPoint(sketch, "E948", {"position": v(33.98, -106.32) * mm});
            skPoint(sketch, "E949", {"position": v(36.3, -106.32) * mm});
            skPoint(sketch, "E950", {"position": v(38.61, -106.32) * mm});
            skPoint(sketch, "E951", {"position": v(43.15, -106.32) * mm});
            skPoint(sketch, "E952", {"position": v(0.02, -108.34) * mm});
            skPoint(sketch, "E953", {"position": v(2.54, -108.34) * mm});
            skPoint(sketch, "E954", {"position": v(5.16, -108.34) * mm});
            skPoint(sketch, "E955", {"position": v(7.8, -108.34) * mm});
            skPoint(sketch, "E956", {"position": v(10.47, -108.34) * mm});
            skPoint(sketch, "E957", {"position": v(15.56, -108.34) * mm});
            skPoint(sketch, "E958", {"position": v(20.13, -108.34) * mm});
            skPoint(sketch, "E959", {"position": v(24.7, -108.34) * mm});
            skPoint(sketch, "E960", {"position": v(29.34, -108.34) * mm});
            skPoint(sketch, "E961", {"position": v(31.67, -108.34) * mm});
            skPoint(sketch, "E962", {"position": v(43.15, -108.34) * mm});
            skLineSegment(sketch, "E963", {"start": v(15.56, -71.59) * mm, "end": v(20.13, -71.59) * mm});
            skLineSegment(sketch, "E964", {"start": v(24.74, -71.59) * mm, "end": v(29.33, -71.59) * mm});
            skLineSegment(sketch, "E965", {"start": v(43.15, -71.59) * mm, "end": v(43.15, -71.59) * mm});
            skLineSegment(sketch, "E966", {"start": v(15.56, -71.59) * mm, "end": v(15.56, -81.78) * mm});
            skLineSegment(sketch, "E967", {"start": v(20.13, -71.59) * mm, "end": v(20.13, -81.78) * mm});
            skLineSegment(sketch, "E968", {"start": v(29.33, -71.59) * mm, "end": v(29.34, -81.78) * mm});
            skLineSegment(sketch, "E969", {"start": v(43.15, -71.59) * mm, "end": v(43.15, -81.84) * mm});
            skLineSegment(sketch, "E970", {"start": v(24.75, -83.84) * mm, "end": v(29.34, -83.84) * mm});
            skLineSegment(sketch, "E971", {"start": v(15.56, -83.84) * mm, "end": v(20.13, -83.84) * mm});
            skLineSegment(sketch, "E972", {"start": v(31.57, -94) * mm, "end": v(36.2, -94) * mm});
            skLineSegment(sketch, "E973", {"start": v(38.52, -94) * mm, "end": v(43.15, -94.07) * mm});
            skLineSegment(sketch, "E974", {"start": v(31.67, -71.59) * mm, "end": v(31.67, -81.78) * mm});
            skLineSegment(sketch, "E975", {"start": v(31.57, -83.84) * mm, "end": v(31.57, -94) * mm});
            skLineSegment(sketch, "E976", {"start": v(31.57, -83.84) * mm, "end": v(36.2, -83.84) * mm});
            skLineSegment(sketch, "E977", {"start": v(38.52, -83.84) * mm, "end": v(43.15, -83.84) * mm});
            skLineSegment(sketch, "E978", {"start": v(38.52, -83.84) * mm, "end": v(38.52, -94) * mm});
            skPoint(sketch, "E979", {"position": v(24.71, -96.04) * mm});
            skPoint(sketch, "E980", {"position": v(29.35, -96.1) * mm});
            skPoint(sketch, "E981", {"position": v(36.24, -96.1) * mm});
            skPoint(sketch, "E982", {"position": v(38.58, -96.1) * mm});
            skPoint(sketch, "E983", {"position": v(43.15, -96.1) * mm});
            skLineSegment(sketch, "E984", {"start": v(36.3, -71.59) * mm, "end": v(36.3, -81.78) * mm});
            skLineSegment(sketch, "E985", {"start": v(36.2, -83.84) * mm, "end": v(36.2, -94) * mm});
            skLineSegment(sketch, "E986", {"start": v(24.71, -96.04) * mm, "end": v(24.7, -106.28) * mm});
            skLineSegment(sketch, "E987", {"start": v(29.35, -96.1) * mm, "end": v(29.3, -106.32) * mm});
            skLineSegment(sketch, "E988", {"start": v(24.71, -96.04) * mm, "end": v(29.35, -96.1) * mm});
            skLineSegment(sketch, "E989", {"start": v(24.7, -106.28) * mm, "end": v(29.3, -106.32) * mm});
            skLineSegment(sketch, "E990", {"start": v(38.58, -96.1) * mm, "end": v(38.61, -106.32) * mm});
            skLineSegment(sketch, "E991", {"start": v(38.58, -96.1) * mm, "end": v(43.15, -96.1) * mm});
            skLineSegment(sketch, "E992", {"start": v(43.15, -106.32) * mm, "end": v(38.61, -106.32) * mm});
            skLineSegment(sketch, "E993", {"start": v(36.24, -96.1) * mm, "end": v(36.3, -106.32) * mm});
            skLineSegment(sketch, "E994", {"start": v(31.67, -106.28) * mm, "end": v(31.64, -96.04) * mm});
            skLineSegment(sketch, "E995", {"start": v(31.64, -96.04) * mm, "end": v(36.24, -96.1) * mm});
            skLineSegment(sketch, "E996", {"start": v(31.67, -106.28) * mm, "end": v(36.3, -106.32) * mm});
            skLineSegment(sketch, "E997", {"start": v(15.56, -108.34) * mm, "end": v(15.6, -118.54) * mm});
            skLineSegment(sketch, "E998", {"start": v(15.6, -118.54) * mm, "end": v(20.1, -118.56) * mm});
            skLineSegment(sketch, "E999", {"start": v(20.1, -118.56) * mm, "end": v(20.13, -108.34) * mm});
            skLineSegment(sketch, "E1000", {"start": v(15.56, -108.34) * mm, "end": v(20.13, -108.34) * mm});
            skLineSegment(sketch, "E1001", {"start": v(24.7, -108.34) * mm, "end": v(29.34, -108.34) * mm});
            skLineSegment(sketch, "E1002", {"start": v(29.35, -118.58) * mm, "end": v(24.72, -118.58) * mm});
            skLineSegment(sketch, "E1003", {"start": v(24.7, -108.34) * mm, "end": v(24.72, -118.58) * mm});
            skLineSegment(sketch, "E1004", {"start": v(29.34, -108.34) * mm, "end": v(29.35, -118.58) * mm});
            skPoint(sketch, "E1005", {"position": v(52.3, -83.81) * mm});
            skPoint(sketch, "E1006", {"position": v(47.76, -94.06) * mm});
            skPoint(sketch, "E1007", {"position": v(52.34, -94.06) * mm});
            skPoint(sketch, "E1008", {"position": v(47.76, -96.08) * mm});
            skPoint(sketch, "E1009", {"position": v(52.36, -96.08) * mm});
            skPoint(sketch, "E1010", {"position": v(47.76, -106.34) * mm});
            skPoint(sketch, "E1011", {"position": v(52.36, -106.34) * mm});
            skPoint(sketch, "E1012", {"position": v(47.76, -108.34) * mm});
            skPoint(sketch, "E1013", {"position": v(52.36, -108.34) * mm});
            skPoint(sketch, "E1014", {"position": v(36.2, -108.35) * mm});
            skPoint(sketch, "E1015", {"position": v(38.52, -108.31) * mm});
            skPoint(sketch, "E1016", {"position": v(31.64, -118.58) * mm});
            skPoint(sketch, "E1017", {"position": v(36.2, -118.58) * mm});
            skPoint(sketch, "E1018", {"position": v(47.7, -118.58) * mm});
            skPoint(sketch, "E1019", {"position": v(52.34, -118.58) * mm});
            skLineSegment(sketch, "E1020", {"start": v(31.64, -118.58) * mm, "end": v(36.2, -118.58) * mm});
            skLineSegment(sketch, "E1021", {"start": v(38.46, -118.58) * mm, "end": v(43.15, -118.58) * mm});
            skLineSegment(sketch, "E1022", {"start": v(47.7, -118.58) * mm, "end": v(52.34, -118.58) * mm});
            skLineSegment(sketch, "E1023", {"start": v(31.67, -108.34) * mm, "end": v(36.2, -108.35) * mm});
            skLineSegment(sketch, "E1024", {"start": v(31.67, -108.34) * mm, "end": v(31.64, -118.58) * mm});
            skLineSegment(sketch, "E1025", {"start": v(36.2, -108.35) * mm, "end": v(36.2, -118.58) * mm});
            skLineSegment(sketch, "E1026", {"start": v(38.52, -108.31) * mm, "end": v(38.46, -118.58) * mm});
            skLineSegment(sketch, "E1027", {"start": v(43.15, -118.58) * mm, "end": v(43.15, -108.34) * mm});
            skLineSegment(sketch, "E1028", {"start": v(43.15, -108.34) * mm, "end": v(38.52, -108.31) * mm});
            skLineSegment(sketch, "E1029", {"start": v(47.76, -108.34) * mm, "end": v(52.36, -108.34) * mm});
            skLineSegment(sketch, "E1030", {"start": v(52.34, -118.58) * mm, "end": v(47.7, -118.58) * mm});
            skLineSegment(sketch, "E1031", {"start": v(47.7, -118.58) * mm, "end": v(47.76, -108.34) * mm});
            skLineSegment(sketch, "E1032", {"start": v(52.36, -108.34) * mm, "end": v(52.34, -118.58) * mm});
            skLineSegment(sketch, "E1033", {"start": v(47.76, -96.08) * mm, "end": v(52.36, -96.08) * mm});
            skLineSegment(sketch, "E1034", {"start": v(52.36, -106.34) * mm, "end": v(52.36, -96.08) * mm});
            skLineSegment(sketch, "E1035", {"start": v(47.76, -96.08) * mm, "end": v(47.76, -106.34) * mm});
            skLineSegment(sketch, "E1036", {"start": v(47.76, -106.34) * mm, "end": v(47.76, -96.08) * mm});
            skLineSegment(sketch, "E1037", {"start": v(47.76, -106.34) * mm, "end": v(52.36, -106.34) * mm});
            skLineSegment(sketch, "E1038", {"start": v(47.76, -83.84) * mm, "end": v(47.76, -94.06) * mm});
            skLineSegment(sketch, "E1039", {"start": v(52.34, -94.06) * mm, "end": v(52.3, -83.81) * mm});
            skLineSegment(sketch, "E1040", {"start": v(52.3, -83.81) * mm, "end": v(52.34, -94.06) * mm});
            skLineSegment(sketch, "E1041", {"start": v(52.34, -94.06) * mm, "end": v(47.76, -94.06) * mm});
            skLineSegment(sketch, "E1042", {"start": v(47.76, -83.84) * mm, "end": v(52.3, -83.81) * mm});
            skPoint(sketch, "E1043", {"position": v(47.86, -67.98) * mm});
            skPoint(sketch, "E1044", {"position": v(38.52, -81.81) * mm});
            skPoint(sketch, "E1045", {"position": v(47.85, -71.53) * mm});
            skPoint(sketch, "E1046", {"position": v(52.42, -71.6) * mm});
            skPoint(sketch, "E1047", {"position": v(47.87, -81.81) * mm});
            skPoint(sketch, "E1048", {"position": v(52.47, -81.83) * mm});
            skPoint(sketch, "E1049", {"position": v(38.52, -71.59) * mm});
            skLineSegment(sketch, "E1050", {"start": v(38.52, -71.59) * mm, "end": v(43.15, -71.59) * mm});
            skLineSegment(sketch, "E1051", {"start": v(38.52, -71.59) * mm, "end": v(38.52, -81.81) * mm});
            skLineSegment(sketch, "E1052", {"start": v(38.52, -81.81) * mm, "end": v(43.15, -81.84) * mm});
            skLineSegment(sketch, "E1053", {"start": v(47.85, -71.53) * mm, "end": v(52.42, -71.6) * mm});
            skLineSegment(sketch, "E1054", {"start": v(52.47, -81.83) * mm, "end": v(47.87, -81.81) * mm});
            skLineSegment(sketch, "E1055", {"start": v(47.85, -71.53) * mm, "end": v(47.87, -81.81) * mm});
            skLineSegment(sketch, "E1056", {"start": v(52.42, -71.6) * mm, "end": v(52.47, -81.83) * mm});
            skLineSegment(sketch, "E1057", {"start": v(52.46, -67.98) * mm, "end": v(57.5, -67.99) * mm});
            skLineSegment(sketch, "E1058", {"start": v(15.3, -67.98) * mm, "end": v(10.47, -67.98) * mm});
            skLineSegment(sketch, "E1059", {"start": v(10.47, -67.98) * mm, "end": v(31.57, -67.98) * mm});
            skLineSegment(sketch, "E1060", {"start": v(36.2, -67.98) * mm, "end": v(57.5, -67.99) * mm});
            skPoint(sketch, "E1061", {"position": v(31.55, -69.55) * mm});
            skPoint(sketch, "E1062", {"position": v(36.2, -69.55) * mm});
            skLineSegment(sketch, "E1063", {"start": v(31.57, -67.98) * mm, "end": v(31.55, -69.55) * mm});
            skLineSegment(sketch, "E1064", {"start": v(36.2, -67.98) * mm, "end": v(36.2, -69.55) * mm});
            skLineSegment(sketch, "E1065", {"start": v(36.2, -69.55) * mm, "end": v(31.55, -69.55) * mm});
            skLineSegment(sketch, "E1066", {"start": v(43.15, -67.99) * mm, "end": v(57.5, -67.99) * mm});
            skLineSegment(sketch, "E1067", {"start": v(-8, -67.98) * mm, "end": v(-5.35, -67.98) * mm});
            skLineSegment(sketch, "E1068", {"start": v(5.25, -67.98) * mm, "end": v(7.82, -67.98) * mm});
            skPoint(sketch, "E1069", {"position": v(0.02, -83.84) * mm});
            skPoint(sketch, "E1070", {"position": v(-20.04, -72) * mm});
            skPoint(sketch, "E1071", {"position": v(-15.54, -71.93) * mm});
            skLineSegment(sketch, "E1072", {"start": v(-20.04, -72) * mm, "end": v(-15.54, -71.93) * mm});
            skLineSegment(sketch, "E1073", {"start": v(-15.54, -71.93) * mm, "end": v(-15.53, -81.8) * mm});
            skLineSegment(sketch, "E1074", {"start": v(-20.04, -72) * mm, "end": v(-20.08, -81.8) * mm});
            skPoint(sketch, "E1075", {"position": v(-8, -108.35) * mm});
            skPoint(sketch, "E1076", {"position": v(-5.35, -108.35) * mm});
            skPoint(sketch, "E1077", {"position": v(-2.72, -108.34) * mm});
            skPoint(sketch, "E1078", {"position": v(-10.44, -108.35) * mm});
            skLineSegment(sketch, "E1079", {"start": v(43.15, -83.84) * mm, "end": v(43.15, -94.07) * mm});
            skLineSegment(sketch, "E1080", {"start": v(43.15, -96.1) * mm, "end": v(43.15, -106.32) * mm});
            skPoint(sketch, "E1081", {"position": v(0.02, -106.3) * mm});
            skPoint(sketch, "E1082", {"position": v(-10.45, -81.8) * mm});
            skPoint(sketch, "E1083", {"position": v(-8, -81.8) * mm});
            skPoint(sketch, "E1084", {"position": v(-5.35, -81.8) * mm});
            skPoint(sketch, "E1085", {"position": v(-2.72, -81.8) * mm});
            skPoint(sketch, "E1086", {"position": v(0, -81.8) * mm});
            skPoint(sketch, "E1087", {"position": v(2.53, -81.8) * mm});
            skPoint(sketch, "E1088", {"position": v(5.16, -81.8) * mm});
            skPoint(sketch, "E1089", {"position": v(7.8, -81.8) * mm});
            skPoint(sketch, "E1090", {"position": v(10.47, -81.8) * mm});
            skPoint(sketch, "E1091", {"position": v(-10.44, -94.1) * mm});
            skPoint(sketch, "E1092", {"position": v(-8, -94.09) * mm});
            skPoint(sketch, "E1093", {"position": v(-5.35, -94.08) * mm});
            skPoint(sketch, "E1094", {"position": v(-2.72, -94.1) * mm});
            skPoint(sketch, "E1095", {"position": v(0.02, -94.1) * mm});
            skPoint(sketch, "E1096", {"position": v(2.53, -94.1) * mm});
            skPoint(sketch, "E1097", {"position": v(5.16, -94.1) * mm});
            skPoint(sketch, "E1098", {"position": v(7.8, -94.1) * mm});
            skPoint(sketch, "E1099", {"position": v(10.48, -94.1) * mm});
            skLineSegment(sketch, "E1100", {"start": v(-2.72, -81.8) * mm, "end": v(2.53, -81.8) * mm});
            skLineSegment(sketch, "E1101", {"start": v(-2.72, -67.98) * mm, "end": v(-2.72, -81.8) * mm});
            skLineSegment(sketch, "E1102", {"start": v(-10.45, -81.8) * mm, "end": v(-8, -81.8) * mm});
            skLineSegment(sketch, "E1103", {"start": v(2.57, -67.98) * mm, "end": v(2.53, -81.8) * mm});
            skLineSegment(sketch, "E1104", {"start": v(-10.44, -83.84) * mm, "end": v(-8, -83.84) * mm});
            skLineSegment(sketch, "E1105", {"start": v(-10.44, -94.1) * mm, "end": v(-8, -94.09) * mm});
            skLineSegment(sketch, "E1106", {"start": v(-2.72, -83.84) * mm, "end": v(2.53, -83.84) * mm});
            skLineSegment(sketch, "E1107", {"start": v(2.53, -94.1) * mm, "end": v(-2.72, -94.1) * mm});
            skLineSegment(sketch, "E1108", {"start": v(-2.72, -83.84) * mm, "end": v(-2.72, -94.1) * mm});
            skLineSegment(sketch, "E1109", {"start": v(2.53, -83.84) * mm, "end": v(2.53, -94.1) * mm});
            skPoint(sketch, "E1110", {"position": v(-2.74, -106.32) * mm});
            skPoint(sketch, "E1111", {"position": v(2.52, -106.33) * mm});
            skPoint(sketch, "E1112", {"position": v(-10.44, -96.04) * mm});
            skPoint(sketch, "E1113", {"position": v(-5.35, -96.04) * mm});
            skPoint(sketch, "E1114", {"position": v(-2.76, -96.04) * mm});
            skPoint(sketch, "E1115", {"position": v(2.59, -96.04) * mm});
            skPoint(sketch, "E1116", {"position": v(5.16, -96.04) * mm});
            skPoint(sketch, "E1117", {"position": v(10.48, -96.04) * mm});
            skPoint(sketch, "E1118", {"position": v(10.48, -106.26) * mm});
            skPoint(sketch, "E1119", {"position": v(5.16, -106.26) * mm});
            skPoint(sketch, "E1120", {"position": v(-5.35, -106.26) * mm});
            skPoint(sketch, "E1121", {"position": v(-10.44, -106.26) * mm});
            skPoint(sketch, "E1122", {"position": v(7.8, -96.07) * mm});
            skPoint(sketch, "E1123", {"position": v(7.8, -106.34) * mm});
            skLineSegment(sketch, "E1124", {"start": v(-8, -83.84) * mm, "end": v(-8, -94.09) * mm});
            skLineSegment(sketch, "E1125", {"start": v(-10.44, -94.1) * mm, "end": v(-10.44, -83.84) * mm});
            skLineSegment(sketch, "E1126", {"start": v(-10.44, -96.04) * mm, "end": v(-10.44, -106.26) * mm});
            skLineSegment(sketch, "E1127", {"start": v(-8, -106.26) * mm, "end": v(-8.02, -96.04) * mm});
            skLineSegment(sketch, "E1128", {"start": v(-8.02, -96.04) * mm, "end": v(-10.44, -96.04) * mm});
            skLineSegment(sketch, "E1129", {"start": v(-10.44, -108.35) * mm, "end": v(-10.41, -118.5) * mm});
            skLineSegment(sketch, "E1130", {"start": v(-10.41, -118.5) * mm, "end": v(-8, -118.5) * mm});
            skLineSegment(sketch, "E1131", {"start": v(-8, -118.5) * mm, "end": v(-8, -108.35) * mm});
            skLineSegment(sketch, "E1132", {"start": v(-2.76, -96.04) * mm, "end": v(2.59, -96.04) * mm});
            skLineSegment(sketch, "E1133", {"start": v(2.59, -96.04) * mm, "end": v(2.52, -106.33) * mm});
            skLineSegment(sketch, "E1134", {"start": v(2.55, -106.27) * mm, "end": v(-2.74, -106.32) * mm});
            skLineSegment(sketch, "E1135", {"start": v(-2.74, -106.32) * mm, "end": v(-2.76, -96.04) * mm});
            skLineSegment(sketch, "E1136", {"start": v(-2.72, -108.34) * mm, "end": v(2.54, -108.34) * mm});
            skLineSegment(sketch, "E1137", {"start": v(-2.72, -118.6) * mm, "end": v(-2.72, -108.34) * mm});
            skPoint(sketch, "E1138", {"position": v(2.52, -118.6) * mm});
            skLineSegment(sketch, "E1139", {"start": v(-2.72, -118.6) * mm, "end": v(2.52, -118.6) * mm});
            skLineSegment(sketch, "E1140", {"start": v(2.52, -118.6) * mm, "end": v(2.54, -108.34) * mm});
            skLineSegment(sketch, "E1141", {"start": v(-10.44, -106.26) * mm, "end": v(-8, -106.26) * mm});
            skLineSegment(sketch, "E1142", {"start": v(-10.44, -108.35) * mm, "end": v(-8, -108.35) * mm});
            skLineSegment(sketch, "E1143", {"start": v(7.8, -83.84) * mm, "end": v(10.48, -83.84) * mm});
            skLineSegment(sketch, "E1144", {"start": v(7.8, -94.1) * mm, "end": v(10.48, -94.1) * mm});
            skLineSegment(sketch, "E1145", {"start": v(7.8, -81.8) * mm, "end": v(10.47, -81.8) * mm});
            skLineSegment(sketch, "E1146", {"start": v(7.8, -96.07) * mm, "end": v(10.48, -96.04) * mm});
            skLineSegment(sketch, "E1147", {"start": v(7.8, -106.34) * mm, "end": v(10.48, -106.26) * mm});
            skLineSegment(sketch, "E1148", {"start": v(10.48, -83.84) * mm, "end": v(10.48, -94.1) * mm});
            skLineSegment(sketch, "E1149", {"start": v(10.48, -96.04) * mm, "end": v(10.48, -106.26) * mm});
            skLineSegment(sketch, "E1150", {"start": v(10.47, -108.34) * mm, "end": v(10.47, -118.4) * mm});
            skLineSegment(sketch, "E1151", {"start": v(7.8, -108.34) * mm, "end": v(10.47, -108.34) * mm});
            skLineSegment(sketch, "E1152", {"start": v(10.47, -118.4) * mm, "end": v(7.8, -118.47) * mm});
            skLineSegment(sketch, "E1153", {"start": v(-10.45, -67.98) * mm, "end": v(-10.45, -81.8) * mm});
            skLineSegment(sketch, "E1154", {"start": v(10.47, -67.98) * mm, "end": v(10.47, -81.8) * mm});
            skLineSegment(sketch, "E1155", {"start": v(8.02, -67.98) * mm, "end": v(7.8, -81.8) * mm});
            skLineSegment(sketch, "E1156", {"start": v(7.8, -83.84) * mm, "end": v(7.8, -94.1) * mm});
            skLineSegment(sketch, "E1157", {"start": v(7.8, -96.07) * mm, "end": v(7.8, -106.34) * mm});
            skLineSegment(sketch, "E1158", {"start": v(7.8, -108.34) * mm, "end": v(7.8, -118.47) * mm});
            skPoint(sketch, "E1159", {"position": v(-8.04, -74.66) * mm});
            skLineSegment(sketch, "E1160", {"start": v(-8.04, -74.66) * mm, "end": v(-8, -81.8) * mm});
            skLineSegment(sketch, "E1161", {"start": v(-8, -81.8) * mm, "end": v(-8.04, -74.66) * mm});
            skPoint(sketch, "E1162", {"position": v(3.98, -52.76) * mm});
            skPoint(sketch, "E1163", {"position": v(4.28, -52.07) * mm});
            skPoint(sketch, "E1164", {"position": v(64.56, 6.22) * mm});
            skSolve(sketch);
        }
        {
            var Q0;
            {var subQ0=sQuery(id+"F1.wireOp",EDGE,"E110");Q0=makeQuery(id+"F1.imprint","IMPRINT",FACE,{"disambiguationData":[TD([[makeQuery(id+"F1.imprint","IMPRINT",EDGE,{"derivedFrom":subQ0}),1.0]])]});}
            var Q1;
            {var subQ14=sQuery(id+"F7.wireOp",EDGE,"E652.right");Q1=makeQuery(id+"F7.imprint","IMPRINT",FACE,{"disambiguationData":[TD([[makeQuery(id+"F7.imprint","IMPRINT",EDGE,{"derivedFrom":subQ14}),1.0]])]});}
            var Q2;
            {var subQ11=sQuery(id+"F7.wireOp",EDGE,"pZeGjCGm-WElQ-uWf7-oS4G-AgP7iqahi8NO");Q2=makeQuery(id+"F7.imprint","IMPRINT",FACE,{"disambiguationData":[TD([[makeQuery(id+"F7.imprint","IMPRINT",EDGE,{"derivedFrom":subQ11}),1.0]])]});}
            var Q3;
            {var subQ0=sQuery(id+"F7.wireOp",EDGE,"E873");var subQ1=sQuery(id+"F7.wireOp",EDGE,"E691");var subQ2=makeQuery(id+"F7.imprint","INTERSECT",VERTEX,{"derivedFrom":[subQ1,subQ0]});Q3=makeQuery(id+"F7.imprint","IMPRINT",FACE,{"disambiguationData":[TD([[makeQuery(id+"F7.imprint","IMPRINT",EDGE,{"disambiguationData":[TD([[subQ2,-1.0]])],"derivedFrom":subQ1}),-1.0]])]});}
            var Q4;
            {var subQ0=sQuery(id+"F7.wireOp",EDGE,"E872");var subQ1=sQuery(id+"F7.wireOp",EDGE,"E691");var subQ2=makeQuery(id+"F7.imprint","INTERSECT",VERTEX,{"derivedFrom":[subQ1,subQ0]});Q4=makeQuery(id+"F7.imprint","IMPRINT",FACE,{"disambiguationData":[TD([[makeQuery(id+"F7.imprint","IMPRINT",EDGE,{"disambiguationData":[TD([[subQ2,-1.0]])],"derivedFrom":subQ1}),-1.0]])]});}
            var Q5;
            {var subQ0=sQuery(id+"F7.wireOp",EDGE,"E870");var subQ1=sQuery(id+"F7.wireOp",EDGE,"E691");var subQ2=makeQuery(id+"F7.imprint","INTERSECT",VERTEX,{"derivedFrom":[subQ1,subQ0]});Q5=makeQuery(id+"F7.imprint","IMPRINT",FACE,{"disambiguationData":[TD([[makeQuery(id+"F7.imprint","IMPRINT",EDGE,{"disambiguationData":[TD([[subQ2,-1.0]])],"derivedFrom":subQ1}),-1.0]])]});}
            var Q6;
            {var subQ0=sQuery(id+"F7.wireOp",EDGE,"E871");var subQ1=sQuery(id+"F7.wireOp",EDGE,"E691");var subQ2=makeQuery(id+"F7.imprint","INTERSECT",VERTEX,{"derivedFrom":[subQ1,subQ0]});Q6=makeQuery(id+"F7.imprint","IMPRINT",FACE,{"disambiguationData":[TD([[makeQuery(id+"F7.imprint","IMPRINT",EDGE,{"disambiguationData":[TD([[subQ2,-1.0]])],"derivedFrom":subQ1}),-1.0]])]});}
            var Q7;
            {var subQ0=sQuery(id+"F7.wireOp",EDGE,"E1059");var subQ1=sQuery(id+"F7.wireOp",EDGE,"E691");var subQ2=makeQuery(id+"F7.imprint","INTERSECT",VERTEX,{"derivedFrom":[subQ1,subQ0]});Q7=makeQuery(id+"F7.imprint","IMPRINT",FACE,{"disambiguationData":[TD([[makeQuery(id+"F7.imprint","IMPRINT",EDGE,{"disambiguationData":[TD([[subQ2,-1.0]])],"derivedFrom":subQ1}),-1.0]])]});}
            var Q8;
            {var subQ0=sQuery(id+"F7.wireOp",EDGE,"E869");var subQ1=sQuery(id+"F7.wireOp",EDGE,"E691");var subQ2=makeQuery(id+"F7.imprint","INTERSECT",VERTEX,{"derivedFrom":[subQ1,subQ0]});Q8=makeQuery(id+"F7.imprint","IMPRINT",FACE,{"disambiguationData":[TD([[makeQuery(id+"F7.imprint","IMPRINT",EDGE,{"disambiguationData":[TD([[subQ2,-1.0]])],"derivedFrom":subQ1}),-1.0]])]});}
            var Q9;
            {var subQ0=sQuery(id+"F7.wireOp",EDGE,"E868");var subQ1=sQuery(id+"F7.wireOp",EDGE,"E691");var subQ2=makeQuery(id+"F7.imprint","INTERSECT",VERTEX,{"derivedFrom":[subQ1,subQ0]});Q9=makeQuery(id+"F7.imprint","IMPRINT",FACE,{"disambiguationData":[TD([[makeQuery(id+"F7.imprint","IMPRINT",EDGE,{"disambiguationData":[TD([[subQ2,-1.0]])],"derivedFrom":subQ1}),-1.0]])]});}
            var Q10;
            {var subQ0=sQuery(id+"F7.wireOp",EDGE,"E1060");var subQ1=sQuery(id+"F7.wireOp",EDGE,"E691");var subQ2=makeQuery(id+"F7.imprint","INTERSECT",VERTEX,{"derivedFrom":[subQ1,subQ0]});Q10=makeQuery(id+"F7.imprint","IMPRINT",FACE,{"disambiguationData":[TD([[makeQuery(id+"F7.imprint","IMPRINT",EDGE,{"disambiguationData":[TD([[subQ2,1.0]])],"derivedFrom":subQ1}),-1.0]])]});}
            var Q11;
            {var subQ4=sQuery(id+"F7.wireOp",EDGE,"E652.left");Q11=makeQuery(id+"F7.imprint","IMPRINT",FACE,{"disambiguationData":[TD([[makeQuery(id+"F7.imprint","IMPRINT",EDGE,{"derivedFrom":subQ4}),-1.0]])]});}
            extrude(context, id + "F8", {"entities" : qUnion([Q0, Q1, Q2, Q3, Q4, Q5, Q6, Q7, Q8, Q9, Q10, Q11]), "operationType" : NewBodyOperationType.ADD, "depth" : 4 * mm, "offsetDistance" : 25 * mm});
        }
    });
